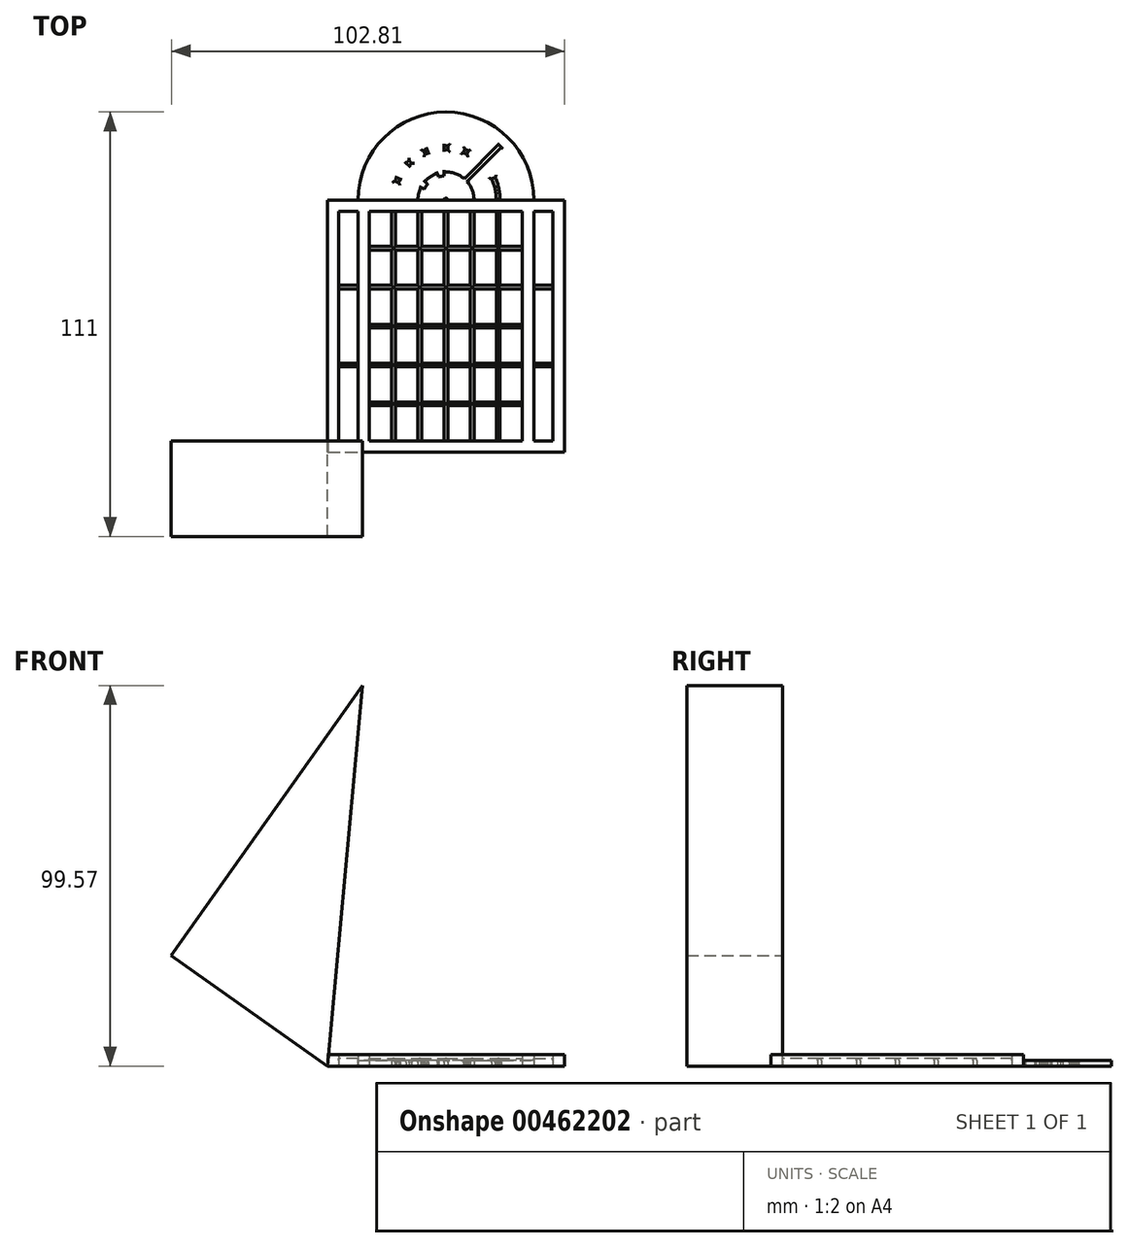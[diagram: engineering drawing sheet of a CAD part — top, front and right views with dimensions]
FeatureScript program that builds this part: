
annotation { "Feature Type Name" : "Feature", "Feature Type Description" : "" }
export const myFeature = defineFeature(function(context is Context, id is Id, definition is map)
    precondition{}
    {
        {
            var Q0;
            Q0=qCreatedBy(makeId("Top.planeOp"),FACE);
            var sketch = newSketch(context, id + "F0", { "sketchPlane" : qUnion([Q0])});
            skLineSegment(sketch, "E0.bottom", {"start": v(0, 0) * mm, "end": v(62, 0) * mm});
            skLineSegment(sketch, "E0.top", {"start": v(0, 60) * mm, "end": v(62, 60) * mm});
            skLineSegment(sketch, "E0.left", {"start": v(0, 0) * mm, "end": v(0, 60) * mm});
            skLineSegment(sketch, "E0.right", {"start": v(62, 0) * mm, "end": v(62, 60) * mm});
            skLineSegment(sketch, "E1", {"start": v(0, 0) * mm, "end": v(8, 0) * mm, "construction": true});
            skLineSegment(sketch, "E2", {"start": v(62, 0) * mm, "end": v(54, 0) * mm, "construction": true});
            skLineSegment(sketch, "E3", {"start": v(62, 0) * mm, "end": v(59, 0) * mm, "construction": true});
            skLineSegment(sketch, "E4", {"start": v(59, 0) * mm, "end": v(59, 60) * mm});
            skLineSegment(sketch, "E5", {"start": v(0, 60) * mm, "end": v(3, 60) * mm, "construction": true});
            skLineSegment(sketch, "E6", {"start": v(3, 60) * mm, "end": v(3, 0) * mm});
            skLineSegment(sketch, "E7", {"start": v(8, 0) * mm, "end": v(8, 60) * mm});
            skLineSegment(sketch, "E8", {"start": v(54, 0) * mm, "end": v(54, 60) * mm});
            skLineSegment(sketch, "E9", {"start": v(8, 0) * mm, "end": v(11, 0) * mm, "construction": true});
            skLineSegment(sketch, "E10", {"start": v(54, 0) * mm, "end": v(51, 0) * mm, "construction": true});
            skLineSegment(sketch, "E11", {"start": v(11, 0) * mm, "end": v(11, 60) * mm});
            skLineSegment(sketch, "E12", {"start": v(51, 0) * mm, "end": v(51, 60) * mm});
            skLineSegment(sketch, "E13.bottom", {"start": v(51, 0) * mm, "end": v(45.17, 0) * mm});
            skLineSegment(sketch, "E13.top", {"start": v(51, 9.17) * mm, "end": v(45.17, 9.17) * mm});
            skLineSegment(sketch, "E13.left", {"start": v(51, 0) * mm, "end": v(51, 9.17) * mm});
            skLineSegment(sketch, "E13.right", {"start": v(45.17, 0) * mm, "end": v(45.17, 9.17) * mm});
            skLineSegment(sketch, "E14.bottom", {"start": v(45.17, 0) * mm, "end": v(44.17, 0) * mm});
            skLineSegment(sketch, "E14.top", {"start": v(45.17, 9.17) * mm, "end": v(44.17, 9.17) * mm, "construction": true});
            skLineSegment(sketch, "E14.right", {"start": v(44.17, 0) * mm, "end": v(44.17, 9.17) * mm});
            skLineSegment(sketch, "E15.top", {"start": v(51, 10.17) * mm, "end": v(45.17, 10.17) * mm});
            skLineSegment(sketch, "E15.left", {"start": v(51, 9.17) * mm, "end": v(51, 10.17) * mm});
            skLineSegment(sketch, "E15.right", {"start": v(45.17, 9.17) * mm, "end": v(45.17, 10.17) * mm, "construction": true});
            skLineSegment(sketch, "E16", {"start": v(44.17, 9.17) * mm, "end": v(44.17, 10.17) * mm, "construction": true});
            skLineSegment(sketch, "E17", {"start": v(44.17, 10.17) * mm, "end": v(45.17, 10.17) * mm, "construction": true});
            skLineSegment(sketch, "E18.0.1.0", {"start": v(44.17, 20.33) * mm, "end": v(45.17, 20.33) * mm, "construction": true});
            skLineSegment(sketch, "E18.0.1.1", {"start": v(51, 20.33) * mm, "end": v(45.17, 20.33) * mm});
            skLineSegment(sketch, "E18.0.1.2", {"start": v(51, 19.33) * mm, "end": v(45.17, 19.33) * mm});
            skLineSegment(sketch, "E18.0.1.3", {"start": v(45.17, 10.17) * mm, "end": v(45.17, 19.33) * mm});
            skLineSegment(sketch, "E18.0.1.4", {"start": v(44.17, 10.17) * mm, "end": v(44.17, 19.33) * mm});
            skLineSegment(sketch, "E18.0.1.5", {"start": v(45.17, 19.33) * mm, "end": v(44.17, 19.33) * mm, "construction": true});
            skLineSegment(sketch, "E18.0.1.6", {"start": v(44.17, 19.33) * mm, "end": v(44.17, 20.33) * mm, "construction": true});
            skLineSegment(sketch, "E18.0.1.7", {"start": v(45.17, 19.33) * mm, "end": v(45.17, 20.33) * mm, "construction": true});
            skLineSegment(sketch, "E18.0.2.0", {"start": v(44.17, 30.5) * mm, "end": v(45.17, 30.5) * mm, "construction": true});
            skLineSegment(sketch, "E18.0.2.1", {"start": v(51, 30.5) * mm, "end": v(45.17, 30.5) * mm});
            skLineSegment(sketch, "E18.0.2.2", {"start": v(51, 29.5) * mm, "end": v(45.17, 29.5) * mm});
            skLineSegment(sketch, "E18.0.2.3", {"start": v(45.17, 20.33) * mm, "end": v(45.17, 29.5) * mm});
            skLineSegment(sketch, "E18.0.2.4", {"start": v(44.17, 20.33) * mm, "end": v(44.17, 29.5) * mm});
            skLineSegment(sketch, "E18.0.2.5", {"start": v(45.17, 29.5) * mm, "end": v(44.17, 29.5) * mm, "construction": true});
            skLineSegment(sketch, "E18.0.2.6", {"start": v(44.17, 29.5) * mm, "end": v(44.17, 30.5) * mm, "construction": true});
            skLineSegment(sketch, "E18.0.2.7", {"start": v(45.17, 29.5) * mm, "end": v(45.17, 30.5) * mm, "construction": true});
            skLineSegment(sketch, "E18.0.3.0", {"start": v(44.17, 40.67) * mm, "end": v(45.17, 40.67) * mm, "construction": true});
            skLineSegment(sketch, "E18.0.3.1", {"start": v(51, 40.67) * mm, "end": v(45.17, 40.67) * mm});
            skLineSegment(sketch, "E18.0.3.2", {"start": v(51, 39.67) * mm, "end": v(45.17, 39.67) * mm});
            skLineSegment(sketch, "E18.0.3.3", {"start": v(45.17, 30.5) * mm, "end": v(45.17, 39.67) * mm});
            skLineSegment(sketch, "E18.0.3.4", {"start": v(44.17, 30.5) * mm, "end": v(44.17, 39.67) * mm});
            skLineSegment(sketch, "E18.0.3.5", {"start": v(45.17, 39.67) * mm, "end": v(44.17, 39.67) * mm, "construction": true});
            skLineSegment(sketch, "E18.0.3.6", {"start": v(44.17, 39.67) * mm, "end": v(44.17, 40.67) * mm, "construction": true});
            skLineSegment(sketch, "E18.0.3.7", {"start": v(45.17, 39.67) * mm, "end": v(45.17, 40.67) * mm, "construction": true});
            skLineSegment(sketch, "E18.0.4.0", {"start": v(44.17, 50.83) * mm, "end": v(45.17, 50.83) * mm, "construction": true});
            skLineSegment(sketch, "E18.0.4.1", {"start": v(51, 50.83) * mm, "end": v(45.17, 50.83) * mm});
            skLineSegment(sketch, "E18.0.4.2", {"start": v(51, 49.83) * mm, "end": v(45.17, 49.83) * mm});
            skLineSegment(sketch, "E18.0.4.3", {"start": v(45.17, 40.67) * mm, "end": v(45.17, 49.83) * mm});
            skLineSegment(sketch, "E18.0.4.4", {"start": v(44.17, 40.67) * mm, "end": v(44.17, 49.83) * mm});
            skLineSegment(sketch, "E18.0.4.5", {"start": v(45.17, 49.83) * mm, "end": v(44.17, 49.83) * mm, "construction": true});
            skLineSegment(sketch, "E18.0.4.6", {"start": v(44.17, 49.83) * mm, "end": v(44.17, 50.83) * mm, "construction": true});
            skLineSegment(sketch, "E18.0.4.7", {"start": v(45.17, 49.83) * mm, "end": v(45.17, 50.83) * mm, "construction": true});
            skLineSegment(sketch, "E18.0.5.2", {"start": v(51, 60) * mm, "end": v(45.17, 60) * mm});
            skLineSegment(sketch, "E18.0.5.3", {"start": v(45.17, 50.83) * mm, "end": v(45.17, 60) * mm});
            skLineSegment(sketch, "E18.0.5.4", {"start": v(44.17, 50.83) * mm, "end": v(44.17, 60) * mm});
            skLineSegment(sketch, "E18.0.5.5", {"start": v(45.17, 60) * mm, "end": v(44.17, 60) * mm, "construction": true});
            skLineSegment(sketch, "E18.1.0.0", {"start": v(37.33, 10.17) * mm, "end": v(38.33, 10.17) * mm, "construction": true});
            skLineSegment(sketch, "E18.1.0.1", {"start": v(44.17, 10.17) * mm, "end": v(38.33, 10.17) * mm});
            skLineSegment(sketch, "E18.1.0.2", {"start": v(44.17, 9.17) * mm, "end": v(38.33, 9.17) * mm});
            skLineSegment(sketch, "E18.1.0.3", {"start": v(38.33, 0) * mm, "end": v(38.33, 9.17) * mm});
            skLineSegment(sketch, "E18.1.0.4", {"start": v(37.33, 0) * mm, "end": v(37.33, 9.17) * mm});
            skLineSegment(sketch, "E18.1.0.5", {"start": v(38.33, 9.17) * mm, "end": v(37.33, 9.17) * mm, "construction": true});
            skLineSegment(sketch, "E18.1.0.6", {"start": v(37.33, 9.17) * mm, "end": v(37.33, 10.17) * mm, "construction": true});
            skLineSegment(sketch, "E18.1.0.7", {"start": v(38.33, 9.17) * mm, "end": v(38.33, 10.17) * mm, "construction": true});
            skLineSegment(sketch, "E18.1.1.0", {"start": v(37.33, 20.33) * mm, "end": v(38.33, 20.33) * mm, "construction": true});
            skLineSegment(sketch, "E18.1.1.1", {"start": v(44.17, 20.33) * mm, "end": v(38.33, 20.33) * mm});
            skLineSegment(sketch, "E18.1.1.2", {"start": v(44.17, 19.33) * mm, "end": v(38.33, 19.33) * mm});
            skLineSegment(sketch, "E18.1.1.3", {"start": v(38.33, 10.17) * mm, "end": v(38.33, 19.33) * mm});
            skLineSegment(sketch, "E18.1.1.4", {"start": v(37.33, 10.17) * mm, "end": v(37.33, 19.33) * mm});
            skLineSegment(sketch, "E18.1.1.5", {"start": v(38.33, 19.33) * mm, "end": v(37.33, 19.33) * mm, "construction": true});
            skLineSegment(sketch, "E18.1.1.6", {"start": v(37.33, 19.33) * mm, "end": v(37.33, 20.33) * mm, "construction": true});
            skLineSegment(sketch, "E18.1.1.7", {"start": v(38.33, 19.33) * mm, "end": v(38.33, 20.33) * mm, "construction": true});
            skLineSegment(sketch, "E18.1.2.0", {"start": v(37.33, 30.5) * mm, "end": v(38.33, 30.5) * mm, "construction": true});
            skLineSegment(sketch, "E18.1.2.1", {"start": v(44.17, 30.5) * mm, "end": v(38.33, 30.5) * mm});
            skLineSegment(sketch, "E18.1.2.2", {"start": v(44.17, 29.5) * mm, "end": v(38.33, 29.5) * mm});
            skLineSegment(sketch, "E18.1.2.3", {"start": v(38.33, 20.33) * mm, "end": v(38.33, 29.5) * mm});
            skLineSegment(sketch, "E18.1.2.4", {"start": v(37.33, 20.33) * mm, "end": v(37.33, 29.5) * mm});
            skLineSegment(sketch, "E18.1.2.5", {"start": v(38.33, 29.5) * mm, "end": v(37.33, 29.5) * mm, "construction": true});
            skLineSegment(sketch, "E18.1.2.6", {"start": v(37.33, 29.5) * mm, "end": v(37.33, 30.5) * mm, "construction": true});
            skLineSegment(sketch, "E18.1.2.7", {"start": v(38.33, 29.5) * mm, "end": v(38.33, 30.5) * mm, "construction": true});
            skLineSegment(sketch, "E18.1.3.0", {"start": v(37.33, 40.67) * mm, "end": v(38.33, 40.67) * mm, "construction": true});
            skLineSegment(sketch, "E18.1.3.1", {"start": v(44.17, 40.67) * mm, "end": v(38.33, 40.67) * mm});
            skLineSegment(sketch, "E18.1.3.2", {"start": v(44.17, 39.67) * mm, "end": v(38.33, 39.67) * mm});
            skLineSegment(sketch, "E18.1.3.3", {"start": v(38.33, 30.5) * mm, "end": v(38.33, 39.67) * mm});
            skLineSegment(sketch, "E18.1.3.4", {"start": v(37.33, 30.5) * mm, "end": v(37.33, 39.67) * mm});
            skLineSegment(sketch, "E18.1.3.5", {"start": v(38.33, 39.67) * mm, "end": v(37.33, 39.67) * mm, "construction": true});
            skLineSegment(sketch, "E18.1.3.6", {"start": v(37.33, 39.67) * mm, "end": v(37.33, 40.67) * mm, "construction": true});
            skLineSegment(sketch, "E18.1.3.7", {"start": v(38.33, 39.67) * mm, "end": v(38.33, 40.67) * mm, "construction": true});
            skLineSegment(sketch, "E18.1.4.0", {"start": v(37.33, 50.83) * mm, "end": v(38.33, 50.83) * mm, "construction": true});
            skLineSegment(sketch, "E18.1.4.1", {"start": v(44.17, 50.83) * mm, "end": v(38.33, 50.83) * mm});
            skLineSegment(sketch, "E18.1.4.2", {"start": v(44.17, 49.83) * mm, "end": v(38.33, 49.83) * mm});
            skLineSegment(sketch, "E18.1.4.3", {"start": v(38.33, 40.67) * mm, "end": v(38.33, 49.83) * mm});
            skLineSegment(sketch, "E18.1.4.4", {"start": v(37.33, 40.67) * mm, "end": v(37.33, 49.83) * mm});
            skLineSegment(sketch, "E18.1.4.5", {"start": v(38.33, 49.83) * mm, "end": v(37.33, 49.83) * mm, "construction": true});
            skLineSegment(sketch, "E18.1.4.6", {"start": v(37.33, 49.83) * mm, "end": v(37.33, 50.83) * mm, "construction": true});
            skLineSegment(sketch, "E18.1.4.7", {"start": v(38.33, 49.83) * mm, "end": v(38.33, 50.83) * mm, "construction": true});
            skLineSegment(sketch, "E18.1.5.2", {"start": v(44.17, 60) * mm, "end": v(38.33, 60) * mm});
            skLineSegment(sketch, "E18.1.5.3", {"start": v(38.33, 50.83) * mm, "end": v(38.33, 60) * mm});
            skLineSegment(sketch, "E18.1.5.4", {"start": v(37.33, 50.83) * mm, "end": v(37.33, 60) * mm});
            skLineSegment(sketch, "E18.1.5.5", {"start": v(38.33, 60) * mm, "end": v(37.33, 60) * mm, "construction": true});
            skLineSegment(sketch, "E18.2.0.0", {"start": v(30.5, 10.17) * mm, "end": v(31.5, 10.17) * mm, "construction": true});
            skLineSegment(sketch, "E18.2.0.1", {"start": v(37.33, 10.17) * mm, "end": v(31.5, 10.17) * mm});
            skLineSegment(sketch, "E18.2.0.2", {"start": v(37.33, 9.17) * mm, "end": v(31.5, 9.17) * mm});
            skLineSegment(sketch, "E18.2.0.3", {"start": v(31.5, 0) * mm, "end": v(31.5, 9.17) * mm});
            skLineSegment(sketch, "E18.2.0.4", {"start": v(30.5, 0) * mm, "end": v(30.5, 9.17) * mm});
            skLineSegment(sketch, "E18.2.0.5", {"start": v(31.5, 9.17) * mm, "end": v(30.5, 9.17) * mm, "construction": true});
            skLineSegment(sketch, "E18.2.0.6", {"start": v(30.5, 9.17) * mm, "end": v(30.5, 10.17) * mm, "construction": true});
            skLineSegment(sketch, "E18.2.0.7", {"start": v(31.5, 9.17) * mm, "end": v(31.5, 10.17) * mm, "construction": true});
            skLineSegment(sketch, "E18.2.1.0", {"start": v(30.5, 20.33) * mm, "end": v(31.5, 20.33) * mm, "construction": true});
            skLineSegment(sketch, "E18.2.1.1", {"start": v(37.33, 20.33) * mm, "end": v(31.5, 20.33) * mm});
            skLineSegment(sketch, "E18.2.1.2", {"start": v(37.33, 19.33) * mm, "end": v(31.5, 19.33) * mm});
            skLineSegment(sketch, "E18.2.1.3", {"start": v(31.5, 10.17) * mm, "end": v(31.5, 19.33) * mm});
            skLineSegment(sketch, "E18.2.1.4", {"start": v(30.5, 10.17) * mm, "end": v(30.5, 19.33) * mm});
            skLineSegment(sketch, "E18.2.1.5", {"start": v(31.5, 19.33) * mm, "end": v(30.5, 19.33) * mm, "construction": true});
            skLineSegment(sketch, "E18.2.1.6", {"start": v(30.5, 19.33) * mm, "end": v(30.5, 20.33) * mm, "construction": true});
            skLineSegment(sketch, "E18.2.1.7", {"start": v(31.5, 19.33) * mm, "end": v(31.5, 20.33) * mm, "construction": true});
            skLineSegment(sketch, "E18.2.2.0", {"start": v(30.5, 30.5) * mm, "end": v(31.5, 30.5) * mm, "construction": true});
            skLineSegment(sketch, "E18.2.2.1", {"start": v(37.33, 30.5) * mm, "end": v(31.5, 30.5) * mm});
            skLineSegment(sketch, "E18.2.2.2", {"start": v(37.33, 29.5) * mm, "end": v(31.5, 29.5) * mm});
            skLineSegment(sketch, "E18.2.2.3", {"start": v(31.5, 20.33) * mm, "end": v(31.5, 29.5) * mm});
            skLineSegment(sketch, "E18.2.2.4", {"start": v(30.5, 20.33) * mm, "end": v(30.5, 29.5) * mm});
            skLineSegment(sketch, "E18.2.2.5", {"start": v(31.5, 29.5) * mm, "end": v(30.5, 29.5) * mm, "construction": true});
            skLineSegment(sketch, "E18.2.2.6", {"start": v(30.5, 29.5) * mm, "end": v(30.5, 30.5) * mm, "construction": true});
            skLineSegment(sketch, "E18.2.2.7", {"start": v(31.5, 29.5) * mm, "end": v(31.5, 30.5) * mm, "construction": true});
            skLineSegment(sketch, "E18.2.3.0", {"start": v(30.5, 40.67) * mm, "end": v(31.5, 40.67) * mm, "construction": true});
            skLineSegment(sketch, "E18.2.3.1", {"start": v(37.33, 40.67) * mm, "end": v(31.5, 40.67) * mm});
            skLineSegment(sketch, "E18.2.3.2", {"start": v(37.33, 39.67) * mm, "end": v(31.5, 39.67) * mm});
            skLineSegment(sketch, "E18.2.3.3", {"start": v(31.5, 30.5) * mm, "end": v(31.5, 39.67) * mm});
            skLineSegment(sketch, "E18.2.3.4", {"start": v(30.5, 30.5) * mm, "end": v(30.5, 39.67) * mm});
            skLineSegment(sketch, "E18.2.3.5", {"start": v(31.5, 39.67) * mm, "end": v(30.5, 39.67) * mm, "construction": true});
            skLineSegment(sketch, "E18.2.3.6", {"start": v(30.5, 39.67) * mm, "end": v(30.5, 40.67) * mm, "construction": true});
            skLineSegment(sketch, "E18.2.3.7", {"start": v(31.5, 39.67) * mm, "end": v(31.5, 40.67) * mm, "construction": true});
            skLineSegment(sketch, "E18.2.4.0", {"start": v(30.5, 50.83) * mm, "end": v(31.5, 50.83) * mm, "construction": true});
            skLineSegment(sketch, "E18.2.4.1", {"start": v(37.33, 50.83) * mm, "end": v(31.5, 50.83) * mm});
            skLineSegment(sketch, "E18.2.4.2", {"start": v(37.33, 49.83) * mm, "end": v(31.5, 49.83) * mm});
            skLineSegment(sketch, "E18.2.4.3", {"start": v(31.5, 40.67) * mm, "end": v(31.5, 49.83) * mm});
            skLineSegment(sketch, "E18.2.4.4", {"start": v(30.5, 40.67) * mm, "end": v(30.5, 49.83) * mm});
            skLineSegment(sketch, "E18.2.4.5", {"start": v(31.5, 49.83) * mm, "end": v(30.5, 49.83) * mm, "construction": true});
            skLineSegment(sketch, "E18.2.4.6", {"start": v(30.5, 49.83) * mm, "end": v(30.5, 50.83) * mm, "construction": true});
            skLineSegment(sketch, "E18.2.4.7", {"start": v(31.5, 49.83) * mm, "end": v(31.5, 50.83) * mm, "construction": true});
            skLineSegment(sketch, "E18.2.5.2", {"start": v(37.33, 60) * mm, "end": v(31.5, 60) * mm});
            skLineSegment(sketch, "E18.2.5.3", {"start": v(31.5, 50.83) * mm, "end": v(31.5, 60) * mm});
            skLineSegment(sketch, "E18.2.5.4", {"start": v(30.5, 50.83) * mm, "end": v(30.5, 60) * mm});
            skLineSegment(sketch, "E18.2.5.5", {"start": v(31.5, 60) * mm, "end": v(30.5, 60) * mm, "construction": true});
            skLineSegment(sketch, "E18.3.0.0", {"start": v(23.67, 10.17) * mm, "end": v(24.67, 10.17) * mm, "construction": true});
            skLineSegment(sketch, "E18.3.0.1", {"start": v(30.5, 10.17) * mm, "end": v(24.67, 10.17) * mm});
            skLineSegment(sketch, "E18.3.0.2", {"start": v(30.5, 9.17) * mm, "end": v(24.67, 9.17) * mm});
            skLineSegment(sketch, "E18.3.0.3", {"start": v(24.67, 0) * mm, "end": v(24.67, 9.17) * mm});
            skLineSegment(sketch, "E18.3.0.4", {"start": v(23.67, 0) * mm, "end": v(23.67, 9.17) * mm});
            skLineSegment(sketch, "E18.3.0.5", {"start": v(24.67, 9.17) * mm, "end": v(23.67, 9.17) * mm, "construction": true});
            skLineSegment(sketch, "E18.3.0.6", {"start": v(23.67, 9.17) * mm, "end": v(23.67, 10.17) * mm, "construction": true});
            skLineSegment(sketch, "E18.3.0.7", {"start": v(24.67, 9.17) * mm, "end": v(24.67, 10.17) * mm, "construction": true});
            skLineSegment(sketch, "E18.3.1.0", {"start": v(23.67, 20.33) * mm, "end": v(24.67, 20.33) * mm, "construction": true});
            skLineSegment(sketch, "E18.3.1.1", {"start": v(30.5, 20.33) * mm, "end": v(24.67, 20.33) * mm});
            skLineSegment(sketch, "E18.3.1.2", {"start": v(30.5, 19.33) * mm, "end": v(24.67, 19.33) * mm});
            skLineSegment(sketch, "E18.3.1.3", {"start": v(24.67, 10.17) * mm, "end": v(24.67, 19.33) * mm});
            skLineSegment(sketch, "E18.3.1.4", {"start": v(23.67, 10.17) * mm, "end": v(23.67, 19.33) * mm});
            skLineSegment(sketch, "E18.3.1.5", {"start": v(24.67, 19.33) * mm, "end": v(23.67, 19.33) * mm, "construction": true});
            skLineSegment(sketch, "E18.3.1.6", {"start": v(23.67, 19.33) * mm, "end": v(23.67, 20.33) * mm, "construction": true});
            skLineSegment(sketch, "E18.3.1.7", {"start": v(24.67, 19.33) * mm, "end": v(24.67, 20.33) * mm, "construction": true});
            skLineSegment(sketch, "E18.3.2.0", {"start": v(23.67, 30.5) * mm, "end": v(24.67, 30.5) * mm, "construction": true});
            skLineSegment(sketch, "E18.3.2.1", {"start": v(30.5, 30.5) * mm, "end": v(24.67, 30.5) * mm});
            skLineSegment(sketch, "E18.3.2.2", {"start": v(30.5, 29.5) * mm, "end": v(24.67, 29.5) * mm});
            skLineSegment(sketch, "E18.3.2.3", {"start": v(24.67, 20.33) * mm, "end": v(24.67, 29.5) * mm});
            skLineSegment(sketch, "E18.3.2.4", {"start": v(23.67, 20.33) * mm, "end": v(23.67, 29.5) * mm});
            skLineSegment(sketch, "E18.3.2.5", {"start": v(24.67, 29.5) * mm, "end": v(23.67, 29.5) * mm, "construction": true});
            skLineSegment(sketch, "E18.3.2.6", {"start": v(23.67, 29.5) * mm, "end": v(23.67, 30.5) * mm, "construction": true});
            skLineSegment(sketch, "E18.3.2.7", {"start": v(24.67, 29.5) * mm, "end": v(24.67, 30.5) * mm, "construction": true});
            skLineSegment(sketch, "E18.3.3.0", {"start": v(23.67, 40.67) * mm, "end": v(24.67, 40.67) * mm, "construction": true});
            skLineSegment(sketch, "E18.3.3.1", {"start": v(30.5, 40.67) * mm, "end": v(24.67, 40.67) * mm});
            skLineSegment(sketch, "E18.3.3.2", {"start": v(30.5, 39.67) * mm, "end": v(24.67, 39.67) * mm});
            skLineSegment(sketch, "E18.3.3.3", {"start": v(24.67, 30.5) * mm, "end": v(24.67, 39.67) * mm});
            skLineSegment(sketch, "E18.3.3.4", {"start": v(23.67, 30.5) * mm, "end": v(23.67, 39.67) * mm});
            skLineSegment(sketch, "E18.3.3.5", {"start": v(24.67, 39.67) * mm, "end": v(23.67, 39.67) * mm, "construction": true});
            skLineSegment(sketch, "E18.3.3.6", {"start": v(23.67, 39.67) * mm, "end": v(23.67, 40.67) * mm, "construction": true});
            skLineSegment(sketch, "E18.3.3.7", {"start": v(24.67, 39.67) * mm, "end": v(24.67, 40.67) * mm, "construction": true});
            skLineSegment(sketch, "E18.3.4.0", {"start": v(23.67, 50.83) * mm, "end": v(24.67, 50.83) * mm, "construction": true});
            skLineSegment(sketch, "E18.3.4.1", {"start": v(30.5, 50.83) * mm, "end": v(24.67, 50.83) * mm});
            skLineSegment(sketch, "E18.3.4.2", {"start": v(30.5, 49.83) * mm, "end": v(24.67, 49.83) * mm});
            skLineSegment(sketch, "E18.3.4.3", {"start": v(24.67, 40.67) * mm, "end": v(24.67, 49.83) * mm});
            skLineSegment(sketch, "E18.3.4.4", {"start": v(23.67, 40.67) * mm, "end": v(23.67, 49.83) * mm});
            skLineSegment(sketch, "E18.3.4.5", {"start": v(24.67, 49.83) * mm, "end": v(23.67, 49.83) * mm, "construction": true});
            skLineSegment(sketch, "E18.3.4.6", {"start": v(23.67, 49.83) * mm, "end": v(23.67, 50.83) * mm, "construction": true});
            skLineSegment(sketch, "E18.3.4.7", {"start": v(24.67, 49.83) * mm, "end": v(24.67, 50.83) * mm, "construction": true});
            skLineSegment(sketch, "E18.3.5.2", {"start": v(30.5, 60) * mm, "end": v(24.67, 60) * mm});
            skLineSegment(sketch, "E18.3.5.3", {"start": v(24.67, 50.83) * mm, "end": v(24.67, 60) * mm});
            skLineSegment(sketch, "E18.3.5.4", {"start": v(23.67, 50.83) * mm, "end": v(23.67, 60) * mm});
            skLineSegment(sketch, "E18.3.5.5", {"start": v(24.67, 60) * mm, "end": v(23.67, 60) * mm, "construction": true});
            skLineSegment(sketch, "E18.4.0.0", {"start": v(16.83, 10.17) * mm, "end": v(17.83, 10.17) * mm, "construction": true});
            skLineSegment(sketch, "E18.4.0.1", {"start": v(23.67, 10.17) * mm, "end": v(17.83, 10.17) * mm});
            skLineSegment(sketch, "E18.4.0.2", {"start": v(23.67, 9.17) * mm, "end": v(17.83, 9.17) * mm});
            skLineSegment(sketch, "E18.4.0.3", {"start": v(17.83, 0) * mm, "end": v(17.83, 9.17) * mm});
            skLineSegment(sketch, "E18.4.0.4", {"start": v(16.83, 0) * mm, "end": v(16.83, 9.17) * mm});
            skLineSegment(sketch, "E18.4.0.5", {"start": v(17.83, 9.17) * mm, "end": v(16.83, 9.17) * mm, "construction": true});
            skLineSegment(sketch, "E18.4.0.6", {"start": v(16.83, 9.17) * mm, "end": v(16.83, 10.17) * mm, "construction": true});
            skLineSegment(sketch, "E18.4.0.7", {"start": v(17.83, 9.17) * mm, "end": v(17.83, 10.17) * mm, "construction": true});
            skLineSegment(sketch, "E18.4.1.0", {"start": v(16.83, 20.33) * mm, "end": v(17.83, 20.33) * mm, "construction": true});
            skLineSegment(sketch, "E18.4.1.1", {"start": v(23.67, 20.33) * mm, "end": v(17.83, 20.33) * mm});
            skLineSegment(sketch, "E18.4.1.2", {"start": v(23.67, 19.33) * mm, "end": v(17.83, 19.33) * mm});
            skLineSegment(sketch, "E18.4.1.3", {"start": v(17.83, 10.17) * mm, "end": v(17.83, 19.33) * mm});
            skLineSegment(sketch, "E18.4.1.4", {"start": v(16.83, 10.17) * mm, "end": v(16.83, 19.33) * mm});
            skLineSegment(sketch, "E18.4.1.5", {"start": v(17.83, 19.33) * mm, "end": v(16.83, 19.33) * mm, "construction": true});
            skLineSegment(sketch, "E18.4.1.6", {"start": v(16.83, 19.33) * mm, "end": v(16.83, 20.33) * mm, "construction": true});
            skLineSegment(sketch, "E18.4.1.7", {"start": v(17.83, 19.33) * mm, "end": v(17.83, 20.33) * mm, "construction": true});
            skLineSegment(sketch, "E18.4.2.0", {"start": v(16.83, 30.5) * mm, "end": v(17.83, 30.5) * mm, "construction": true});
            skLineSegment(sketch, "E18.4.2.1", {"start": v(23.67, 30.5) * mm, "end": v(17.83, 30.5) * mm});
            skLineSegment(sketch, "E18.4.2.2", {"start": v(23.67, 29.5) * mm, "end": v(17.83, 29.5) * mm});
            skLineSegment(sketch, "E18.4.2.3", {"start": v(17.83, 20.33) * mm, "end": v(17.83, 29.5) * mm});
            skLineSegment(sketch, "E18.4.2.4", {"start": v(16.83, 20.33) * mm, "end": v(16.83, 29.5) * mm});
            skLineSegment(sketch, "E18.4.2.5", {"start": v(17.83, 29.5) * mm, "end": v(16.83, 29.5) * mm, "construction": true});
            skLineSegment(sketch, "E18.4.2.6", {"start": v(16.83, 29.5) * mm, "end": v(16.83, 30.5) * mm, "construction": true});
            skLineSegment(sketch, "E18.4.2.7", {"start": v(17.83, 29.5) * mm, "end": v(17.83, 30.5) * mm, "construction": true});
            skLineSegment(sketch, "E18.4.3.0", {"start": v(16.83, 40.67) * mm, "end": v(17.83, 40.67) * mm, "construction": true});
            skLineSegment(sketch, "E18.4.3.1", {"start": v(23.67, 40.67) * mm, "end": v(17.83, 40.67) * mm});
            skLineSegment(sketch, "E18.4.3.2", {"start": v(23.67, 39.67) * mm, "end": v(17.83, 39.67) * mm});
            skLineSegment(sketch, "E18.4.3.3", {"start": v(17.83, 30.5) * mm, "end": v(17.83, 39.67) * mm});
            skLineSegment(sketch, "E18.4.3.4", {"start": v(16.83, 30.5) * mm, "end": v(16.83, 39.67) * mm});
            skLineSegment(sketch, "E18.4.3.5", {"start": v(17.83, 39.67) * mm, "end": v(16.83, 39.67) * mm, "construction": true});
            skLineSegment(sketch, "E18.4.3.6", {"start": v(16.83, 39.67) * mm, "end": v(16.83, 40.67) * mm, "construction": true});
            skLineSegment(sketch, "E18.4.3.7", {"start": v(17.83, 39.67) * mm, "end": v(17.83, 40.67) * mm, "construction": true});
            skLineSegment(sketch, "E18.4.4.0", {"start": v(16.83, 50.83) * mm, "end": v(17.83, 50.83) * mm, "construction": true});
            skLineSegment(sketch, "E18.4.4.1", {"start": v(23.67, 50.83) * mm, "end": v(17.83, 50.83) * mm});
            skLineSegment(sketch, "E18.4.4.2", {"start": v(23.67, 49.83) * mm, "end": v(17.83, 49.83) * mm});
            skLineSegment(sketch, "E18.4.4.3", {"start": v(17.83, 40.67) * mm, "end": v(17.83, 49.83) * mm});
            skLineSegment(sketch, "E18.4.4.4", {"start": v(16.83, 40.67) * mm, "end": v(16.83, 49.83) * mm});
            skLineSegment(sketch, "E18.4.4.5", {"start": v(17.83, 49.83) * mm, "end": v(16.83, 49.83) * mm, "construction": true});
            skLineSegment(sketch, "E18.4.4.6", {"start": v(16.83, 49.83) * mm, "end": v(16.83, 50.83) * mm, "construction": true});
            skLineSegment(sketch, "E18.4.4.7", {"start": v(17.83, 49.83) * mm, "end": v(17.83, 50.83) * mm, "construction": true});
            skLineSegment(sketch, "E18.4.5.2", {"start": v(23.67, 60) * mm, "end": v(17.83, 60) * mm});
            skLineSegment(sketch, "E18.4.5.3", {"start": v(17.83, 50.83) * mm, "end": v(17.83, 60) * mm});
            skLineSegment(sketch, "E18.4.5.4", {"start": v(16.83, 50.83) * mm, "end": v(16.83, 60) * mm});
            skLineSegment(sketch, "E18.4.5.5", {"start": v(17.83, 60) * mm, "end": v(16.83, 60) * mm, "construction": true});
            skLineSegment(sketch, "E18.5.0.1", {"start": v(16.83, 10.17) * mm, "end": v(11, 10.17) * mm});
            skLineSegment(sketch, "E18.5.0.2", {"start": v(16.83, 9.17) * mm, "end": v(11, 9.17) * mm});
            skLineSegment(sketch, "E18.5.0.3", {"start": v(11, 0) * mm, "end": v(11, 9.17) * mm});
            skLineSegment(sketch, "E18.5.0.7", {"start": v(11, 9.17) * mm, "end": v(11, 10.17) * mm, "construction": true});
            skLineSegment(sketch, "E18.5.1.1", {"start": v(16.83, 20.33) * mm, "end": v(11, 20.33) * mm});
            skLineSegment(sketch, "E18.5.1.2", {"start": v(16.83, 19.33) * mm, "end": v(11, 19.33) * mm});
            skLineSegment(sketch, "E18.5.1.3", {"start": v(11, 10.17) * mm, "end": v(11, 19.33) * mm});
            skLineSegment(sketch, "E18.5.1.7", {"start": v(11, 19.33) * mm, "end": v(11, 20.33) * mm, "construction": true});
            skLineSegment(sketch, "E18.5.2.1", {"start": v(16.83, 30.5) * mm, "end": v(11, 30.5) * mm});
            skLineSegment(sketch, "E18.5.2.2", {"start": v(16.83, 29.5) * mm, "end": v(11, 29.5) * mm});
            skLineSegment(sketch, "E18.5.2.3", {"start": v(11, 20.33) * mm, "end": v(11, 29.5) * mm});
            skLineSegment(sketch, "E18.5.2.7", {"start": v(11, 29.5) * mm, "end": v(11, 30.5) * mm, "construction": true});
            skLineSegment(sketch, "E18.5.3.1", {"start": v(16.83, 40.67) * mm, "end": v(11, 40.67) * mm});
            skLineSegment(sketch, "E18.5.3.2", {"start": v(16.83, 39.67) * mm, "end": v(11, 39.67) * mm});
            skLineSegment(sketch, "E18.5.3.3", {"start": v(11, 30.5) * mm, "end": v(11, 39.67) * mm});
            skLineSegment(sketch, "E18.5.3.7", {"start": v(11, 39.67) * mm, "end": v(11, 40.67) * mm, "construction": true});
            skLineSegment(sketch, "E18.5.4.1", {"start": v(16.83, 50.83) * mm, "end": v(11, 50.83) * mm});
            skLineSegment(sketch, "E18.5.4.2", {"start": v(16.83, 49.83) * mm, "end": v(11, 49.83) * mm});
            skLineSegment(sketch, "E18.5.4.3", {"start": v(11, 40.67) * mm, "end": v(11, 49.83) * mm});
            skLineSegment(sketch, "E18.5.4.7", {"start": v(11, 49.83) * mm, "end": v(11, 50.83) * mm, "construction": true});
            skLineSegment(sketch, "E18.5.5.2", {"start": v(16.83, 60) * mm, "end": v(11, 60) * mm});
            skLineSegment(sketch, "E18.5.5.3", {"start": v(11, 50.83) * mm, "end": v(11, 60) * mm});
            skLineSegment(sketch, "E18.direction1", {"start": v(44.17, 0) * mm, "end": v(37.33, 0) * mm, "construction": true});
            skLineSegment(sketch, "E18.direction2", {"start": v(44.17, 0) * mm, "end": v(44.17, 10.17) * mm, "construction": true});
            skLineSegment(sketch, "E19.top", {"start": v(0, -3) * mm, "end": v(62, -3) * mm});
            skLineSegment(sketch, "E19.left", {"start": v(0, 0) * mm, "end": v(0, -3) * mm});
            skLineSegment(sketch, "E19.right", {"start": v(62, 0) * mm, "end": v(62, -3) * mm});
            skLineSegment(sketch, "E20.top", {"start": v(0, 63) * mm, "end": v(62, 63) * mm});
            skLineSegment(sketch, "E20.left", {"start": v(0, 60) * mm, "end": v(0, 63) * mm});
            skLineSegment(sketch, "E20.right", {"start": v(62, 60) * mm, "end": v(62, 63) * mm});
            skLineSegment(sketch, "E21", {"start": v(31, 63) * mm, "end": v(31, 86) * mm, "construction": true});
            skArc(sketch, "E22", {"start": v(11, 63) * mm, "mid": v(31, 83) * mm, "end": v(51, 63) * mm});
            skArc(sketch, "E23", {"start": v(8, 63) * mm, "mid": v(31, 86) * mm, "end": v(54, 63) * mm});
            skArc(sketch, "E24", {"start": v(16.83, 63) * mm, "mid": v(31, 77.17) * mm, "end": v(45.17, 63) * mm});
            skArc(sketch, "E25", {"start": v(17.83, 63) * mm, "mid": v(31, 76.17) * mm, "end": v(44.17, 63) * mm});
            skArc(sketch, "E26", {"start": v(23.67, 63) * mm, "mid": v(31, 70.33) * mm, "end": v(38.33, 63) * mm});
            skArc(sketch, "E27", {"start": v(24.67, 63) * mm, "mid": v(31, 69.33) * mm, "end": v(37.33, 63) * mm});
            skArc(sketch, "E28", {"start": v(30.5, 63) * mm, "mid": v(31, 63.5) * mm, "end": v(31.5, 63) * mm});
            skLineSegment(sketch, "E29", {"start": v(31, 63) * mm, "end": v(8, 63) * mm});
            skLineSegment(sketch, "E30.1.0", {"start": v(31, 63) * mm, "end": v(9.75, 71.8) * mm, "construction": true});
            skLineSegment(sketch, "E30.2.0", {"start": v(31, 63) * mm, "end": v(14.74, 79.26) * mm, "construction": true});
            skLineSegment(sketch, "E30.3.0", {"start": v(31, 63) * mm, "end": v(22.2, 84.25) * mm, "construction": true});
            skLineSegment(sketch, "E30.5.0", {"start": v(31, 63) * mm, "end": v(39.8, 84.25) * mm, "construction": true});
            skLineSegment(sketch, "E30.6.0", {"start": v(31, 63) * mm, "end": v(47.26, 79.26) * mm, "construction": true});
            skLineSegment(sketch, "E30.7.0", {"start": v(31, 63) * mm, "end": v(52.25, 71.8) * mm, "construction": true});
            skLineSegment(sketch, "E30.8.0", {"start": v(31, 63) * mm, "end": v(54, 63) * mm});
            skLineSegment(sketch, "E30.anchor1", {"start": v(31, 63) * mm, "end": v(8, 63) * mm, "construction": true});
            skLineSegment(sketch, "E30.anchor2", {"start": v(31, 63) * mm, "end": v(54, 63) * mm, "construction": true});
            skLineSegment(sketch, "E31.0", {"start": v(30.08, 63.92) * mm, "end": v(12.72, 71.11) * mm});
            skLineSegment(sketch, "E32.MirrorCS", {"start": v(29.7, 63) * mm, "end": v(12.34, 70.19) * mm});
            skLineSegment(sketch, "E33.0", {"start": v(30.5, 64.2) * mm, "end": v(17.22, 77.5) * mm});
            skLineSegment(sketch, "E34.MirrorCS", {"start": v(28.87, 64.42) * mm, "end": v(16.5, 76.78) * mm});
            skLineSegment(sketch, "E35.0", {"start": v(31, 64.3) * mm, "end": v(23.81, 81.66) * mm});
            skLineSegment(sketch, "E36.MirrorCS", {"start": v(30.08, 63.92) * mm, "end": v(22.89, 81.28) * mm});
            skLineSegment(sketch, "E37.0", {"start": v(31.5, 65.51) * mm, "end": v(31.5, 83) * mm});
            skLineSegment(sketch, "E38.0", {"start": v(30.5, 65.51) * mm, "end": v(30.5, 83) * mm});
            skLineSegment(sketch, "E39.0", {"start": v(32.42, 65.13) * mm, "end": v(39.11, 81.28) * mm});
            skLineSegment(sketch, "E40.0", {"start": v(31, 64.3) * mm, "end": v(38.19, 81.66) * mm});
            skLineSegment(sketch, "E41.0", {"start": v(32.3, 63) * mm, "end": v(49.66, 70.19) * mm});
            skLineSegment(sketch, "E42.0", {"start": v(33.13, 64.42) * mm, "end": v(49.28, 71.11) * mm});
            skLineSegment(sketch, "E43.0", {"start": v(33.13, 64.42) * mm, "end": v(45.5, 76.78) * mm});
            skLineSegment(sketch, "E44.0", {"start": v(32.42, 65.13) * mm, "end": v(44.78, 77.5) * mm});
            skSolve(sketch);
        }
        {
            var Q0;
            {var subQ10=sQuery(id+"F0.wireOp",EDGE,"E23");Q0=makeQuery(id+"F0.imprint","IMPRINT",FACE,{"disambiguationData":[TD([[makeQuery(id+"F0.imprint","IMPRINT",EDGE,{"derivedFrom":subQ10}),-1.0]])]});}
            var Q1;
            {var subQ22=sQuery(id+"F0.wireOp",EDGE,"E20.left");Q1=makeQuery(id+"F0.imprint","IMPRINT",FACE,{"disambiguationData":[TD([[makeQuery(id+"F0.imprint","IMPRINT",EDGE,{"derivedFrom":subQ22}),-1.0]])]});}
            var Q2;
            {var subQ0=sQuery(id+"F0.wireOp",EDGE,"E0.right");Q2=makeQuery(id+"F0.imprint","IMPRINT",FACE,{"disambiguationData":[TD([[makeQuery(id+"F0.imprint","IMPRINT",EDGE,{"derivedFrom":subQ0}),1.0]])]});}
            var Q3;
            {var subQ14=sQuery(id+"F0.wireOp",EDGE,"E7");Q3=makeQuery(id+"F0.imprint","IMPRINT",FACE,{"disambiguationData":[TD([[makeQuery(id+"F0.imprint","IMPRINT",EDGE,{"derivedFrom":subQ14}),-1.0]])]});}
            var Q4;
            {var subQ0=sQuery(id+"F0.wireOp",EDGE,"E0.left");Q4=makeQuery(id+"F0.imprint","IMPRINT",FACE,{"disambiguationData":[TD([[makeQuery(id+"F0.imprint","IMPRINT",EDGE,{"derivedFrom":subQ0}),-1.0]])]});}
            var Q5;
            {var subQ5=sQuery(id+"F0.wireOp",EDGE,"E8");Q5=makeQuery(id+"F0.imprint","IMPRINT",FACE,{"disambiguationData":[TD([[makeQuery(id+"F0.imprint","IMPRINT",EDGE,{"derivedFrom":subQ5}),1.0]])]});}
            var Q6;
            Q6=makeQuery(id+"F0.imprint","IMPRINT",FACE,{"disambiguationData":[TD([[makeQuery(id+"F0.imprint","IMPRINT",EDGE,{"derivedFrom":sQuery(id+"F0.wireOp",EDGE,"E19.top")}),1.0]])]});
            extrude(context, id + "F1", {"entities" : qUnion([Q0, Q1, Q2, Q3, Q4, Q5, Q6]), "depth" : 3 * mm});
        }
        {
            var Q0;
            {var subQ0=sQuery(id+"F0.wireOp",EDGE,"E24");var subQ1=sQuery(id+"F0.wireOp",EDGE,"E20.top");var subQ2=makeQuery(id+"F0.imprint","INTERSECT",VERTEX,{"disambiguationData":[OD(0.0)],"derivedFrom":[subQ1,subQ0]});Q0=makeQuery(id+"F0.imprint","IMPRINT",FACE,{"disambiguationData":[TD([[makeQuery(id+"F0.imprint","IMPRINT",EDGE,{"disambiguationData":[TD([[subQ2,-1.0]])],"derivedFrom":subQ1}),1.0]])]});}
            var Q1;
            {var subQ0=sQuery(id+"F0.wireOp",EDGE,"E31.0");var subQ1=sQuery(id+"F0.wireOp",EDGE,"E24");var subQ2=makeQuery(id+"F0.imprint","INTERSECT",VERTEX,{"derivedFrom":[subQ1,subQ0]});Q1=makeQuery(id+"F0.imprint","IMPRINT",FACE,{"disambiguationData":[TD([[makeQuery(id+"F0.imprint","IMPRINT",EDGE,{"disambiguationData":[TD([[subQ2,-1.0]])],"derivedFrom":subQ1}),-1.0]])]});}
            var Q2;
            {var subQ0=sQuery(id+"F0.wireOp",EDGE,"E35.0");var subQ1=sQuery(id+"F0.wireOp",EDGE,"E24");var subQ2=makeQuery(id+"F0.imprint","INTERSECT",VERTEX,{"derivedFrom":[subQ1,subQ0]});Q2=makeQuery(id+"F0.imprint","IMPRINT",FACE,{"disambiguationData":[TD([[makeQuery(id+"F0.imprint","IMPRINT",EDGE,{"disambiguationData":[TD([[subQ2,-1.0]])],"derivedFrom":subQ1}),-1.0]])]});}
            var Q3;
            {var subQ0=sQuery(id+"F0.wireOp",EDGE,"E37.0");var subQ1=sQuery(id+"F0.wireOp",EDGE,"E24");var subQ2=makeQuery(id+"F0.imprint","INTERSECT",VERTEX,{"derivedFrom":[subQ1,subQ0]});Q3=makeQuery(id+"F0.imprint","IMPRINT",FACE,{"disambiguationData":[TD([[makeQuery(id+"F0.imprint","IMPRINT",EDGE,{"disambiguationData":[TD([[subQ2,-1.0]])],"derivedFrom":subQ1}),-1.0]])]});}
            var Q4;
            {var subQ0=sQuery(id+"F0.wireOp",EDGE,"E39.0");var subQ1=sQuery(id+"F0.wireOp",EDGE,"E24");var subQ2=makeQuery(id+"F0.imprint","INTERSECT",VERTEX,{"derivedFrom":[subQ1,subQ0]});Q4=makeQuery(id+"F0.imprint","IMPRINT",FACE,{"disambiguationData":[TD([[makeQuery(id+"F0.imprint","IMPRINT",EDGE,{"disambiguationData":[TD([[subQ2,-1.0]])],"derivedFrom":subQ1}),-1.0]])]});}
            var Q5;
            {var subQ0=sQuery(id+"F0.wireOp",EDGE,"E42.0");var subQ1=sQuery(id+"F0.wireOp",EDGE,"E24");var subQ2=makeQuery(id+"F0.imprint","INTERSECT",VERTEX,{"derivedFrom":[subQ1,subQ0]});Q5=makeQuery(id+"F0.imprint","IMPRINT",FACE,{"disambiguationData":[TD([[makeQuery(id+"F0.imprint","IMPRINT",EDGE,{"disambiguationData":[TD([[subQ2,1.0]])],"derivedFrom":subQ1}),-1.0]])]});}
            var Q6;
            {var subQ0=sQuery(id+"F0.wireOp",EDGE,"E24");var subQ1=sQuery(id+"F0.wireOp",EDGE,"E20.top");var subQ2=makeQuery(id+"F0.imprint","INTERSECT",VERTEX,{"disambiguationData":[OD(1.0)],"derivedFrom":[subQ1,subQ0]});Q6=makeQuery(id+"F0.imprint","IMPRINT",FACE,{"disambiguationData":[TD([[makeQuery(id+"F0.imprint","IMPRINT",EDGE,{"disambiguationData":[TD([[subQ2,1.0]])],"derivedFrom":subQ1}),1.0]])]});}
            var Q7;
            {var subQ0=sQuery(id+"F0.wireOp",EDGE,"E34.MirrorCS");var subQ1=sQuery(id+"F0.wireOp",EDGE,"E22");var subQ2=makeQuery(id+"F0.imprint","INTERSECT",VERTEX,{"derivedFrom":[subQ1,subQ0]});Q7=makeQuery(id+"F0.imprint","IMPRINT",FACE,{"disambiguationData":[TD([[makeQuery(id+"F0.imprint","IMPRINT",EDGE,{"disambiguationData":[TD([[subQ2,-1.0]])],"derivedFrom":subQ1}),-1.0]])]});}
            var Q8;
            {var subQ0=sQuery(id+"F0.wireOp",EDGE,"E32.MirrorCS");var subQ1=sQuery(id+"F0.wireOp",EDGE,"E22");var subQ2=makeQuery(id+"F0.imprint","INTERSECT",VERTEX,{"derivedFrom":[subQ1,subQ0]});Q8=makeQuery(id+"F0.imprint","IMPRINT",FACE,{"disambiguationData":[TD([[makeQuery(id+"F0.imprint","IMPRINT",EDGE,{"disambiguationData":[TD([[subQ2,-1.0]])],"derivedFrom":subQ1}),-1.0]])]});}
            var Q9;
            {var subQ0=sQuery(id+"F0.wireOp",EDGE,"E36.MirrorCS");var subQ1=sQuery(id+"F0.wireOp",EDGE,"E22");var subQ2=makeQuery(id+"F0.imprint","INTERSECT",VERTEX,{"derivedFrom":[subQ1,subQ0]});Q9=makeQuery(id+"F0.imprint","IMPRINT",FACE,{"disambiguationData":[TD([[makeQuery(id+"F0.imprint","IMPRINT",EDGE,{"disambiguationData":[TD([[subQ2,-1.0]])],"derivedFrom":subQ1}),-1.0]])]});}
            var Q10;
            {var subQ0=sQuery(id+"F0.wireOp",EDGE,"E38.0");var subQ1=sQuery(id+"F0.wireOp",EDGE,"E22");var subQ2=makeQuery(id+"F0.imprint","INTERSECT",VERTEX,{"derivedFrom":[subQ1,subQ0]});Q10=makeQuery(id+"F0.imprint","IMPRINT",FACE,{"disambiguationData":[TD([[makeQuery(id+"F0.imprint","IMPRINT",EDGE,{"disambiguationData":[TD([[subQ2,-1.0]])],"derivedFrom":subQ1}),-1.0]])]});}
            var Q11;
            {var subQ0=sQuery(id+"F0.wireOp",EDGE,"E40.0");var subQ1=sQuery(id+"F0.wireOp",EDGE,"E22");var subQ2=makeQuery(id+"F0.imprint","INTERSECT",VERTEX,{"derivedFrom":[subQ1,subQ0]});Q11=makeQuery(id+"F0.imprint","IMPRINT",FACE,{"disambiguationData":[TD([[makeQuery(id+"F0.imprint","IMPRINT",EDGE,{"disambiguationData":[TD([[subQ2,-1.0]])],"derivedFrom":subQ1}),-1.0]])]});}
            var Q12;
            {var subQ0=sQuery(id+"F0.wireOp",EDGE,"E44.0");var subQ1=sQuery(id+"F0.wireOp",EDGE,"E22");var subQ2=makeQuery(id+"F0.imprint","INTERSECT",VERTEX,{"derivedFrom":[subQ1,subQ0]});Q12=makeQuery(id+"F0.imprint","IMPRINT",FACE,{"disambiguationData":[TD([[makeQuery(id+"F0.imprint","IMPRINT",EDGE,{"disambiguationData":[TD([[subQ2,-1.0]])],"derivedFrom":subQ1}),-1.0]])]});}
            var Q13;
            {var subQ0=sQuery(id+"F0.wireOp",EDGE,"E42.0");var subQ1=sQuery(id+"F0.wireOp",EDGE,"E22");var subQ2=makeQuery(id+"F0.imprint","INTERSECT",VERTEX,{"derivedFrom":[subQ1,subQ0]});Q13=makeQuery(id+"F0.imprint","IMPRINT",FACE,{"disambiguationData":[TD([[makeQuery(id+"F0.imprint","IMPRINT",EDGE,{"disambiguationData":[TD([[subQ2,-1.0]])],"derivedFrom":subQ1}),-1.0]])]});}
            var Q14;
            {var subQ0=sQuery(id+"F0.wireOp",EDGE,"E41.0");var subQ1=sQuery(id+"F0.wireOp",EDGE,"E24");var subQ2=makeQuery(id+"F0.imprint","INTERSECT",VERTEX,{"derivedFrom":[subQ1,subQ0]});Q14=makeQuery(id+"F0.imprint","IMPRINT",FACE,{"disambiguationData":[TD([[makeQuery(id+"F0.imprint","IMPRINT",EDGE,{"disambiguationData":[TD([[subQ2,1.0]])],"derivedFrom":subQ1}),-1.0]])]});}
            var Q15;
            {var subQ0=sQuery(id+"F0.wireOp",EDGE,"E43.0");var subQ1=sQuery(id+"F0.wireOp",EDGE,"E24");var subQ2=makeQuery(id+"F0.imprint","INTERSECT",VERTEX,{"derivedFrom":[subQ1,subQ0]});Q15=makeQuery(id+"F0.imprint","IMPRINT",FACE,{"disambiguationData":[TD([[makeQuery(id+"F0.imprint","IMPRINT",EDGE,{"disambiguationData":[TD([[subQ2,1.0]])],"derivedFrom":subQ1}),-1.0]])]});}
            var Q16;
            {var subQ0=sQuery(id+"F0.wireOp",EDGE,"E39.0");var subQ1=sQuery(id+"F0.wireOp",EDGE,"E24");var subQ2=makeQuery(id+"F0.imprint","INTERSECT",VERTEX,{"derivedFrom":[subQ1,subQ0]});Q16=makeQuery(id+"F0.imprint","IMPRINT",FACE,{"disambiguationData":[TD([[makeQuery(id+"F0.imprint","IMPRINT",EDGE,{"disambiguationData":[TD([[subQ2,1.0]])],"derivedFrom":subQ1}),-1.0]])]});}
            var Q17;
            {var subQ0=sQuery(id+"F0.wireOp",EDGE,"E37.0");var subQ1=sQuery(id+"F0.wireOp",EDGE,"E24");var subQ2=makeQuery(id+"F0.imprint","INTERSECT",VERTEX,{"derivedFrom":[subQ1,subQ0]});Q17=makeQuery(id+"F0.imprint","IMPRINT",FACE,{"disambiguationData":[TD([[makeQuery(id+"F0.imprint","IMPRINT",EDGE,{"disambiguationData":[TD([[subQ2,1.0]])],"derivedFrom":subQ1}),-1.0]])]});}
            var Q18;
            {var subQ0=sQuery(id+"F0.wireOp",EDGE,"E35.0");var subQ1=sQuery(id+"F0.wireOp",EDGE,"E24");var subQ2=makeQuery(id+"F0.imprint","INTERSECT",VERTEX,{"derivedFrom":[subQ1,subQ0]});Q18=makeQuery(id+"F0.imprint","IMPRINT",FACE,{"disambiguationData":[TD([[makeQuery(id+"F0.imprint","IMPRINT",EDGE,{"disambiguationData":[TD([[subQ2,1.0]])],"derivedFrom":subQ1}),-1.0]])]});}
            var Q19;
            {var subQ0=sQuery(id+"F0.wireOp",EDGE,"E33.0");var subQ1=sQuery(id+"F0.wireOp",EDGE,"E24");var subQ2=makeQuery(id+"F0.imprint","INTERSECT",VERTEX,{"derivedFrom":[subQ1,subQ0]});Q19=makeQuery(id+"F0.imprint","IMPRINT",FACE,{"disambiguationData":[TD([[makeQuery(id+"F0.imprint","IMPRINT",EDGE,{"disambiguationData":[TD([[subQ2,1.0]])],"derivedFrom":subQ1}),-1.0]])]});}
            var Q20;
            {var subQ0=sQuery(id+"F0.wireOp",EDGE,"E31.0");var subQ1=sQuery(id+"F0.wireOp",EDGE,"E24");var subQ2=makeQuery(id+"F0.imprint","INTERSECT",VERTEX,{"derivedFrom":[subQ1,subQ0]});Q20=makeQuery(id+"F0.imprint","IMPRINT",FACE,{"disambiguationData":[TD([[makeQuery(id+"F0.imprint","IMPRINT",EDGE,{"disambiguationData":[TD([[subQ2,1.0]])],"derivedFrom":subQ1}),-1.0]])]});}
            var Q21;
            {var subQ0=sQuery(id+"F0.wireOp",EDGE,"E32.MirrorCS");var subQ1=sQuery(id+"F0.wireOp",EDGE,"E25");var subQ2=makeQuery(id+"F0.imprint","INTERSECT",VERTEX,{"derivedFrom":[subQ1,subQ0]});Q21=makeQuery(id+"F0.imprint","IMPRINT",FACE,{"disambiguationData":[TD([[makeQuery(id+"F0.imprint","IMPRINT",EDGE,{"disambiguationData":[TD([[subQ2,-1.0]])],"derivedFrom":subQ1}),-1.0]])]});}
            var Q22;
            {var subQ0=sQuery(id+"F0.wireOp",EDGE,"E34.MirrorCS");var subQ1=sQuery(id+"F0.wireOp",EDGE,"E25");var subQ2=makeQuery(id+"F0.imprint","INTERSECT",VERTEX,{"derivedFrom":[subQ1,subQ0]});Q22=makeQuery(id+"F0.imprint","IMPRINT",FACE,{"disambiguationData":[TD([[makeQuery(id+"F0.imprint","IMPRINT",EDGE,{"disambiguationData":[TD([[subQ2,-1.0]])],"derivedFrom":subQ1}),-1.0]])]});}
            var Q23;
            {var subQ0=sQuery(id+"F0.wireOp",EDGE,"E36.MirrorCS");var subQ1=sQuery(id+"F0.wireOp",EDGE,"E25");var subQ2=makeQuery(id+"F0.imprint","INTERSECT",VERTEX,{"derivedFrom":[subQ1,subQ0]});Q23=makeQuery(id+"F0.imprint","IMPRINT",FACE,{"disambiguationData":[TD([[makeQuery(id+"F0.imprint","IMPRINT",EDGE,{"disambiguationData":[TD([[subQ2,-1.0]])],"derivedFrom":subQ1}),-1.0]])]});}
            var Q24;
            {var subQ0=sQuery(id+"F0.wireOp",EDGE,"E38.0");var subQ1=sQuery(id+"F0.wireOp",EDGE,"E25");var subQ2=makeQuery(id+"F0.imprint","INTERSECT",VERTEX,{"derivedFrom":[subQ1,subQ0]});Q24=makeQuery(id+"F0.imprint","IMPRINT",FACE,{"disambiguationData":[TD([[makeQuery(id+"F0.imprint","IMPRINT",EDGE,{"disambiguationData":[TD([[subQ2,-1.0]])],"derivedFrom":subQ1}),-1.0]])]});}
            var Q25;
            {var subQ0=sQuery(id+"F0.wireOp",EDGE,"E40.0");var subQ1=sQuery(id+"F0.wireOp",EDGE,"E25");var subQ2=makeQuery(id+"F0.imprint","INTERSECT",VERTEX,{"derivedFrom":[subQ1,subQ0]});Q25=makeQuery(id+"F0.imprint","IMPRINT",FACE,{"disambiguationData":[TD([[makeQuery(id+"F0.imprint","IMPRINT",EDGE,{"disambiguationData":[TD([[subQ2,-1.0]])],"derivedFrom":subQ1}),-1.0]])]});}
            var Q26;
            {var subQ0=sQuery(id+"F0.wireOp",EDGE,"E44.0");var subQ1=sQuery(id+"F0.wireOp",EDGE,"E25");var subQ2=makeQuery(id+"F0.imprint","INTERSECT",VERTEX,{"derivedFrom":[subQ1,subQ0]});Q26=makeQuery(id+"F0.imprint","IMPRINT",FACE,{"disambiguationData":[TD([[makeQuery(id+"F0.imprint","IMPRINT",EDGE,{"disambiguationData":[TD([[subQ2,-1.0]])],"derivedFrom":subQ1}),-1.0]])]});}
            var Q27;
            {var subQ0=sQuery(id+"F0.wireOp",EDGE,"E42.0");var subQ1=sQuery(id+"F0.wireOp",EDGE,"E25");var subQ2=makeQuery(id+"F0.imprint","INTERSECT",VERTEX,{"derivedFrom":[subQ1,subQ0]});Q27=makeQuery(id+"F0.imprint","IMPRINT",FACE,{"disambiguationData":[TD([[makeQuery(id+"F0.imprint","IMPRINT",EDGE,{"disambiguationData":[TD([[subQ2,-1.0]])],"derivedFrom":subQ1}),-1.0]])]});}
            var Q28;
            {var subQ0=sQuery(id+"F0.wireOp",EDGE,"E26");var subQ1=sQuery(id+"F0.wireOp",EDGE,"E20.top");var subQ2=makeQuery(id+"F0.imprint","INTERSECT",VERTEX,{"disambiguationData":[OD(1.0)],"derivedFrom":[subQ1,subQ0]});Q28=makeQuery(id+"F0.imprint","IMPRINT",FACE,{"disambiguationData":[TD([[makeQuery(id+"F0.imprint","IMPRINT",EDGE,{"disambiguationData":[TD([[subQ2,1.0]])],"derivedFrom":subQ1}),1.0]])]});}
            var Q29;
            {var subQ0=sQuery(id+"F0.wireOp",EDGE,"E41.0");var subQ1=sQuery(id+"F0.wireOp",EDGE,"E26");var subQ2=makeQuery(id+"F0.imprint","INTERSECT",VERTEX,{"derivedFrom":[subQ1,subQ0]});Q29=makeQuery(id+"F0.imprint","IMPRINT",FACE,{"disambiguationData":[TD([[makeQuery(id+"F0.imprint","IMPRINT",EDGE,{"disambiguationData":[TD([[subQ2,1.0]])],"derivedFrom":subQ1}),-1.0]])]});}
            var Q30;
            {var subQ0=sQuery(id+"F0.wireOp",EDGE,"E42.0");var subQ1=sQuery(id+"F0.wireOp",EDGE,"E26");var subQ2=makeQuery(id+"F0.imprint","INTERSECT",VERTEX,{"derivedFrom":[subQ1,subQ0]});Q30=makeQuery(id+"F0.imprint","IMPRINT",FACE,{"disambiguationData":[TD([[makeQuery(id+"F0.imprint","IMPRINT",EDGE,{"disambiguationData":[TD([[subQ2,1.0]])],"derivedFrom":subQ1}),-1.0]])]});}
            var Q31;
            {var subQ0=sQuery(id+"F0.wireOp",EDGE,"E43.0");var subQ1=sQuery(id+"F0.wireOp",EDGE,"E26");var subQ2=makeQuery(id+"F0.imprint","INTERSECT",VERTEX,{"derivedFrom":[subQ1,subQ0]});Q31=makeQuery(id+"F0.imprint","IMPRINT",FACE,{"disambiguationData":[TD([[makeQuery(id+"F0.imprint","IMPRINT",EDGE,{"disambiguationData":[TD([[subQ2,1.0]])],"derivedFrom":subQ1}),-1.0]])]});}
            var Q32;
            {var subQ0=sQuery(id+"F0.wireOp",EDGE,"E39.0");var subQ1=sQuery(id+"F0.wireOp",EDGE,"E26");var subQ2=makeQuery(id+"F0.imprint","INTERSECT",VERTEX,{"derivedFrom":[subQ1,subQ0]});Q32=makeQuery(id+"F0.imprint","IMPRINT",FACE,{"disambiguationData":[TD([[makeQuery(id+"F0.imprint","IMPRINT",EDGE,{"disambiguationData":[TD([[subQ2,-1.0]])],"derivedFrom":subQ1}),-1.0]])]});}
            var Q33;
            {var subQ0=sQuery(id+"F0.wireOp",EDGE,"E39.0");var subQ1=sQuery(id+"F0.wireOp",EDGE,"E26");var subQ2=makeQuery(id+"F0.imprint","INTERSECT",VERTEX,{"derivedFrom":[subQ1,subQ0]});Q33=makeQuery(id+"F0.imprint","IMPRINT",FACE,{"disambiguationData":[TD([[makeQuery(id+"F0.imprint","IMPRINT",EDGE,{"disambiguationData":[TD([[subQ2,1.0]])],"derivedFrom":subQ1}),-1.0]])]});}
            var Q34;
            {var subQ0=sQuery(id+"F0.wireOp",EDGE,"E37.0");var subQ1=sQuery(id+"F0.wireOp",EDGE,"E26");var subQ2=makeQuery(id+"F0.imprint","INTERSECT",VERTEX,{"derivedFrom":[subQ1,subQ0]});Q34=makeQuery(id+"F0.imprint","IMPRINT",FACE,{"disambiguationData":[TD([[makeQuery(id+"F0.imprint","IMPRINT",EDGE,{"disambiguationData":[TD([[subQ2,-1.0]])],"derivedFrom":subQ1}),-1.0]])]});}
            var Q35;
            {var subQ0=sQuery(id+"F0.wireOp",EDGE,"E37.0");var subQ1=sQuery(id+"F0.wireOp",EDGE,"E26");var subQ2=makeQuery(id+"F0.imprint","INTERSECT",VERTEX,{"derivedFrom":[subQ1,subQ0]});Q35=makeQuery(id+"F0.imprint","IMPRINT",FACE,{"disambiguationData":[TD([[makeQuery(id+"F0.imprint","IMPRINT",EDGE,{"disambiguationData":[TD([[subQ2,1.0]])],"derivedFrom":subQ1}),-1.0]])]});}
            var Q36;
            {var subQ0=sQuery(id+"F0.wireOp",EDGE,"E35.0");var subQ1=sQuery(id+"F0.wireOp",EDGE,"E26");var subQ2=makeQuery(id+"F0.imprint","INTERSECT",VERTEX,{"derivedFrom":[subQ1,subQ0]});Q36=makeQuery(id+"F0.imprint","IMPRINT",FACE,{"disambiguationData":[TD([[makeQuery(id+"F0.imprint","IMPRINT",EDGE,{"disambiguationData":[TD([[subQ2,-1.0]])],"derivedFrom":subQ1}),-1.0]])]});}
            var Q37;
            {var subQ0=sQuery(id+"F0.wireOp",EDGE,"E35.0");var subQ1=sQuery(id+"F0.wireOp",EDGE,"E26");var subQ2=makeQuery(id+"F0.imprint","INTERSECT",VERTEX,{"derivedFrom":[subQ1,subQ0]});Q37=makeQuery(id+"F0.imprint","IMPRINT",FACE,{"disambiguationData":[TD([[makeQuery(id+"F0.imprint","IMPRINT",EDGE,{"disambiguationData":[TD([[subQ2,1.0]])],"derivedFrom":subQ1}),-1.0]])]});}
            var Q38;
            {var subQ0=sQuery(id+"F0.wireOp",EDGE,"E33.0");var subQ1=sQuery(id+"F0.wireOp",EDGE,"E26");var subQ2=makeQuery(id+"F0.imprint","INTERSECT",VERTEX,{"derivedFrom":[subQ1,subQ0]});Q38=makeQuery(id+"F0.imprint","IMPRINT",FACE,{"disambiguationData":[TD([[makeQuery(id+"F0.imprint","IMPRINT",EDGE,{"disambiguationData":[TD([[subQ2,-1.0]])],"derivedFrom":subQ1}),-1.0]])]});}
            var Q39;
            {var subQ0=sQuery(id+"F0.wireOp",EDGE,"E33.0");var subQ1=sQuery(id+"F0.wireOp",EDGE,"E26");var subQ2=makeQuery(id+"F0.imprint","INTERSECT",VERTEX,{"derivedFrom":[subQ1,subQ0]});Q39=makeQuery(id+"F0.imprint","IMPRINT",FACE,{"disambiguationData":[TD([[makeQuery(id+"F0.imprint","IMPRINT",EDGE,{"disambiguationData":[TD([[subQ2,1.0]])],"derivedFrom":subQ1}),-1.0]])]});}
            var Q40;
            {var subQ0=sQuery(id+"F0.wireOp",EDGE,"E31.0");var subQ1=sQuery(id+"F0.wireOp",EDGE,"E26");var subQ2=makeQuery(id+"F0.imprint","INTERSECT",VERTEX,{"derivedFrom":[subQ1,subQ0]});Q40=makeQuery(id+"F0.imprint","IMPRINT",FACE,{"disambiguationData":[TD([[makeQuery(id+"F0.imprint","IMPRINT",EDGE,{"disambiguationData":[TD([[subQ2,-1.0]])],"derivedFrom":subQ1}),-1.0]])]});}
            var Q41;
            {var subQ0=sQuery(id+"F0.wireOp",EDGE,"E31.0");var subQ1=sQuery(id+"F0.wireOp",EDGE,"E26");var subQ2=makeQuery(id+"F0.imprint","INTERSECT",VERTEX,{"derivedFrom":[subQ1,subQ0]});Q41=makeQuery(id+"F0.imprint","IMPRINT",FACE,{"disambiguationData":[TD([[makeQuery(id+"F0.imprint","IMPRINT",EDGE,{"disambiguationData":[TD([[subQ2,1.0]])],"derivedFrom":subQ1}),-1.0]])]});}
            var Q42;
            {var subQ0=sQuery(id+"F0.wireOp",EDGE,"E26");var subQ1=sQuery(id+"F0.wireOp",EDGE,"E20.top");var subQ2=makeQuery(id+"F0.imprint","INTERSECT",VERTEX,{"disambiguationData":[OD(0.0)],"derivedFrom":[subQ1,subQ0]});Q42=makeQuery(id+"F0.imprint","IMPRINT",FACE,{"disambiguationData":[TD([[makeQuery(id+"F0.imprint","IMPRINT",EDGE,{"disambiguationData":[TD([[subQ2,-1.0]])],"derivedFrom":subQ1}),1.0]])]});}
            var Q43;
            {var subQ10=sQuery(id+"F0.wireOp",EDGE,"E28");Q43=makeQuery(id+"F0.imprint","IMPRINT",FACE,{"disambiguationData":[TD([[makeQuery(id+"F0.imprint","IMPRINT",EDGE,{"derivedFrom":subQ10}),1.0]])]});}
            var Q44;
            {var subQ0=sQuery(id+"F0.wireOp",EDGE,"E34.MirrorCS");var subQ3=sQuery(id+"F0.wireOp",EDGE,"E27");var subQ4=makeQuery(id+"F0.imprint","INTERSECT",VERTEX,{"derivedFrom":[subQ3,subQ0]});Q44=makeQuery(id+"F0.imprint","IMPRINT",FACE,{"disambiguationData":[TD([[makeQuery(id+"F0.imprint","IMPRINT",EDGE,{"disambiguationData":[TD([[subQ4,-1.0]])],"derivedFrom":subQ3}),-1.0]])]});}
            var Q45;
            {var subQ0=sQuery(id+"F0.wireOp",EDGE,"E38.0");var subQ3=sQuery(id+"F0.wireOp",EDGE,"E27");var subQ4=makeQuery(id+"F0.imprint","INTERSECT",VERTEX,{"derivedFrom":[subQ3,subQ0]});Q45=makeQuery(id+"F0.imprint","IMPRINT",FACE,{"disambiguationData":[TD([[makeQuery(id+"F0.imprint","IMPRINT",EDGE,{"disambiguationData":[TD([[subQ4,-1.0]])],"derivedFrom":subQ3}),-1.0]])]});}
            var Q46;
            {var subQ0=sQuery(id+"F0.wireOp",EDGE,"E33.0");var subQ1=sQuery(id+"F0.wireOp",EDGE,"E24");var subQ2=makeQuery(id+"F0.imprint","INTERSECT",VERTEX,{"derivedFrom":[subQ1,subQ0]});Q46=makeQuery(id+"F0.imprint","IMPRINT",FACE,{"disambiguationData":[TD([[makeQuery(id+"F0.imprint","IMPRINT",EDGE,{"disambiguationData":[TD([[subQ2,-1.0]])],"derivedFrom":subQ1}),-1.0]])]});}
            extrude(context, id + "F2", {"entities" : qUnion([Q0, Q1, Q2, Q3, Q4, Q5, Q6, Q7, Q8, Q9, Q10, Q11, Q12, Q13, Q14, Q15, Q16, Q17, Q18, Q19, Q20, Q21, Q22, Q23, Q24, Q25, Q26, Q27, Q28, Q29, Q30, Q31, Q32, Q33, Q34, Q35, Q36, Q37, Q38, Q39, Q40, Q41, Q42, Q43, Q44, Q45, Q46]), "operationType" : NewBodyOperationType.ADD, "depth" : 1.5 * mm});
        }
        {
            var Q0;
            {var subQ26=sQuery(id+"F0.wireOp",EDGE,"E13.top");Q0=makeQuery(id+"F0.imprint","IMPRINT",FACE,{"disambiguationData":[TD([[makeQuery(id+"F0.imprint","IMPRINT",EDGE,{"derivedFrom":subQ26}),-1.0]])]});}
            extrude(context, id + "F3", {"entities" : qUnion([Q0]), "operationType" : NewBodyOperationType.ADD, "depth" : 2 * mm});
        }
        {
            var Q0;
            Q0=makeQuery(id+"F3.opExtrude","CAP_EDGE",EDGE,{"disambiguationData":[OSD([sQuery(id+"F0.wireOp",EDGE,"E18.4.5.4")])],"isStart":false});
            var Q1;
            Q1=makeQuery(id+"F3.opExtrude","CAP_EDGE",EDGE,{"disambiguationData":[OSD([sQuery(id+"F0.wireOp",EDGE,"E18.4.5.3")])],"isStart":false});
            var Q2;
            Q2=makeQuery(id+"F3.opExtrude","CAP_EDGE",EDGE,{"disambiguationData":[OSD([sQuery(id+"F0.wireOp",EDGE,"E18.3.5.4")])],"isStart":false});
            var Q3;
            Q3=makeQuery(id+"F3.opExtrude","CAP_EDGE",EDGE,{"disambiguationData":[OSD([sQuery(id+"F0.wireOp",EDGE,"E18.3.5.3")])],"isStart":false});
            var Q4;
            Q4=makeQuery(id+"F3.opExtrude","CAP_EDGE",EDGE,{"disambiguationData":[OSD([sQuery(id+"F0.wireOp",EDGE,"E18.2.5.4")])],"isStart":false});
            var Q5;
            Q5=makeQuery(id+"F3.opExtrude","CAP_EDGE",EDGE,{"disambiguationData":[OSD([sQuery(id+"F0.wireOp",EDGE,"E18.2.5.3")])],"isStart":false});
            var Q6;
            Q6=makeQuery(id+"F3.opExtrude","CAP_EDGE",EDGE,{"disambiguationData":[OSD([sQuery(id+"F0.wireOp",EDGE,"E18.1.5.4")])],"isStart":false});
            var Q7;
            Q7=makeQuery(id+"F3.opExtrude","CAP_EDGE",EDGE,{"disambiguationData":[OSD([sQuery(id+"F0.wireOp",EDGE,"E18.1.5.3")])],"isStart":false});
            var Q8;
            Q8=makeQuery(id+"F3.opExtrude","CAP_EDGE",EDGE,{"disambiguationData":[OSD([sQuery(id+"F0.wireOp",EDGE,"E18.1.4.1")])],"isStart":false});
            var Q9;
            Q9=makeQuery(id+"F3.opExtrude","CAP_EDGE",EDGE,{"disambiguationData":[OSD([sQuery(id+"F0.wireOp",EDGE,"E18.1.4.2")])],"isStart":false});
            var Q10;
            Q10=makeQuery(id+"F3.opExtrude","CAP_EDGE",EDGE,{"disambiguationData":[OSD([sQuery(id+"F0.wireOp",EDGE,"E18.1.4.3")])],"isStart":false});
            var Q11;
            Q11=makeQuery(id+"F3.opExtrude","CAP_EDGE",EDGE,{"disambiguationData":[OSD([sQuery(id+"F0.wireOp",EDGE,"E18.1.4.4")])],"isStart":false});
            var Q12;
            Q12=makeQuery(id+"F3.opExtrude","CAP_EDGE",EDGE,{"disambiguationData":[OSD([sQuery(id+"F0.wireOp",EDGE,"E18.2.4.2")])],"isStart":false});
            var Q13;
            Q13=makeQuery(id+"F3.opExtrude","CAP_EDGE",EDGE,{"disambiguationData":[OSD([sQuery(id+"F0.wireOp",EDGE,"E18.2.4.1")])],"isStart":false});
            var Q14;
            Q14=makeQuery(id+"F3.opExtrude","CAP_EDGE",EDGE,{"disambiguationData":[OSD([sQuery(id+"F0.wireOp",EDGE,"E18.3.4.2")])],"isStart":false});
            var Q15;
            Q15=makeQuery(id+"F3.opExtrude","CAP_EDGE",EDGE,{"disambiguationData":[OSD([sQuery(id+"F0.wireOp",EDGE,"E18.3.4.1")])],"isStart":false});
            var Q16;
            Q16=makeQuery(id+"F3.opExtrude","CAP_EDGE",EDGE,{"disambiguationData":[OSD([sQuery(id+"F0.wireOp",EDGE,"E18.4.4.1")])],"isStart":false});
            var Q17;
            Q17=makeQuery(id+"F3.opExtrude","CAP_EDGE",EDGE,{"disambiguationData":[OSD([sQuery(id+"F0.wireOp",EDGE,"E18.4.4.2")])],"isStart":false});
            var Q18;
            Q18=makeQuery(id+"F3.opExtrude","CAP_EDGE",EDGE,{"disambiguationData":[OSD([sQuery(id+"F0.wireOp",EDGE,"E18.5.4.1")])],"isStart":false});
            var Q19;
            Q19=makeQuery(id+"F3.opExtrude","CAP_EDGE",EDGE,{"disambiguationData":[OSD([sQuery(id+"F0.wireOp",EDGE,"E18.5.4.2")])],"isStart":false});
            var Q20;
            Q20=makeQuery(id+"F3.opExtrude","CAP_EDGE",EDGE,{"disambiguationData":[OSD([sQuery(id+"F0.wireOp",EDGE,"E18.4.4.4")])],"isStart":false});
            var Q21;
            Q21=makeQuery(id+"F3.opExtrude","CAP_EDGE",EDGE,{"disambiguationData":[OSD([sQuery(id+"F0.wireOp",EDGE,"E18.4.4.3")])],"isStart":false});
            var Q22;
            Q22=makeQuery(id+"F3.opExtrude","CAP_EDGE",EDGE,{"disambiguationData":[OSD([sQuery(id+"F0.wireOp",EDGE,"E18.4.3.4")])],"isStart":false});
            var Q23;
            Q23=makeQuery(id+"F3.opExtrude","CAP_EDGE",EDGE,{"disambiguationData":[OSD([sQuery(id+"F0.wireOp",EDGE,"E18.4.3.3")])],"isStart":false});
            var Q24;
            Q24=makeQuery(id+"F3.opExtrude","CAP_EDGE",EDGE,{"disambiguationData":[OSD([sQuery(id+"F0.wireOp",EDGE,"E18.3.3.4")])],"isStart":false});
            var Q25;
            Q25=makeQuery(id+"F3.opExtrude","CAP_EDGE",EDGE,{"disambiguationData":[OSD([sQuery(id+"F0.wireOp",EDGE,"E18.3.4.4")])],"isStart":false});
            var Q26;
            Q26=makeQuery(id+"F3.opExtrude","CAP_EDGE",EDGE,{"disambiguationData":[OSD([sQuery(id+"F0.wireOp",EDGE,"E18.3.4.3")])],"isStart":false});
            var Q27;
            Q27=makeQuery(id+"F3.opExtrude","CAP_EDGE",EDGE,{"disambiguationData":[OSD([sQuery(id+"F0.wireOp",EDGE,"E18.2.4.4")])],"isStart":false});
            var Q28;
            Q28=makeQuery(id+"F3.opExtrude","CAP_EDGE",EDGE,{"disambiguationData":[OSD([sQuery(id+"F0.wireOp",EDGE,"E18.2.4.3")])],"isStart":false});
            var Q29;
            Q29=makeQuery(id+"F3.opExtrude","CAP_EDGE",EDGE,{"disambiguationData":[OSD([sQuery(id+"F0.wireOp",EDGE,"E18.2.3.4")])],"isStart":false});
            var Q30;
            Q30=makeQuery(id+"F3.opExtrude","CAP_EDGE",EDGE,{"disambiguationData":[OSD([sQuery(id+"F0.wireOp",EDGE,"E18.2.3.3")])],"isStart":false});
            var Q31;
            Q31=makeQuery(id+"F3.opExtrude","CAP_EDGE",EDGE,{"disambiguationData":[OSD([sQuery(id+"F0.wireOp",EDGE,"E18.1.3.4")])],"isStart":false});
            var Q32;
            Q32=makeQuery(id+"F3.opExtrude","CAP_EDGE",EDGE,{"disambiguationData":[OSD([sQuery(id+"F0.wireOp",EDGE,"E18.1.3.3")])],"isStart":false});
            var Q33;
            Q33=makeQuery(id+"F3.opExtrude","CAP_EDGE",EDGE,{"disambiguationData":[OSD([sQuery(id+"F0.wireOp",EDGE,"E18.0.3.4")])],"isStart":false});
            var Q34;
            Q34=makeQuery(id+"F3.opExtrude","CAP_EDGE",EDGE,{"disambiguationData":[OSD([sQuery(id+"F0.wireOp",EDGE,"E18.0.3.3")])],"isStart":false});
            var Q35;
            Q35=makeQuery(id+"F3.opExtrude","CAP_EDGE",EDGE,{"disambiguationData":[OSD([sQuery(id+"F0.wireOp",EDGE,"E18.0.4.4")])],"isStart":false});
            var Q36;
            Q36=makeQuery(id+"F3.opExtrude","CAP_EDGE",EDGE,{"disambiguationData":[OSD([sQuery(id+"F0.wireOp",EDGE,"E18.0.4.3")])],"isStart":false});
            var Q37;
            Q37=makeQuery(id+"F3.opExtrude","CAP_EDGE",EDGE,{"disambiguationData":[OSD([sQuery(id+"F0.wireOp",EDGE,"E18.0.5.4")])],"isStart":false});
            var Q38;
            Q38=makeQuery(id+"F3.opExtrude","CAP_EDGE",EDGE,{"disambiguationData":[OSD([sQuery(id+"F0.wireOp",EDGE,"E18.0.5.3")])],"isStart":false});
            var Q39;
            Q39=makeQuery(id+"F3.opExtrude","CAP_EDGE",EDGE,{"disambiguationData":[OSD([sQuery(id+"F0.wireOp",EDGE,"E18.0.4.1")])],"isStart":false});
            var Q40;
            Q40=makeQuery(id+"F3.opExtrude","CAP_EDGE",EDGE,{"disambiguationData":[OSD([sQuery(id+"F0.wireOp",EDGE,"E18.0.4.2")])],"isStart":false});
            var Q41;
            Q41=makeQuery(id+"F3.opExtrude","CAP_EDGE",EDGE,{"disambiguationData":[OSD([sQuery(id+"F0.wireOp",EDGE,"E18.0.3.2")])],"isStart":false});
            var Q42;
            Q42=makeQuery(id+"F3.opExtrude","CAP_EDGE",EDGE,{"disambiguationData":[OSD([sQuery(id+"F0.wireOp",EDGE,"E18.0.3.1")])],"isStart":false});
            var Q43;
            Q43=makeQuery(id+"F3.opExtrude","CAP_EDGE",EDGE,{"disambiguationData":[OSD([sQuery(id+"F0.wireOp",EDGE,"E18.1.3.2")])],"isStart":false});
            var Q44;
            Q44=makeQuery(id+"F3.opExtrude","CAP_EDGE",EDGE,{"disambiguationData":[OSD([sQuery(id+"F0.wireOp",EDGE,"E18.1.3.1")])],"isStart":false});
            var Q45;
            Q45=makeQuery(id+"F3.opExtrude","CAP_EDGE",EDGE,{"disambiguationData":[OSD([sQuery(id+"F0.wireOp",EDGE,"E18.2.3.2")])],"isStart":false});
            var Q46;
            Q46=makeQuery(id+"F3.opExtrude","CAP_EDGE",EDGE,{"disambiguationData":[OSD([sQuery(id+"F0.wireOp",EDGE,"E18.2.3.1")])],"isStart":false});
            var Q47;
            Q47=makeQuery(id+"F3.opExtrude","CAP_EDGE",EDGE,{"disambiguationData":[OSD([sQuery(id+"F0.wireOp",EDGE,"E18.3.3.2")])],"isStart":false});
            var Q48;
            Q48=makeQuery(id+"F3.opExtrude","CAP_EDGE",EDGE,{"disambiguationData":[OSD([sQuery(id+"F0.wireOp",EDGE,"E18.3.3.1")])],"isStart":false});
            var Q49;
            Q49=makeQuery(id+"F3.opExtrude","CAP_EDGE",EDGE,{"disambiguationData":[OSD([sQuery(id+"F0.wireOp",EDGE,"E18.4.3.2")])],"isStart":false});
            var Q50;
            Q50=makeQuery(id+"F3.opExtrude","CAP_EDGE",EDGE,{"disambiguationData":[OSD([sQuery(id+"F0.wireOp",EDGE,"E18.4.3.1")])],"isStart":false});
            var Q51;
            Q51=makeQuery(id+"F3.opExtrude","CAP_EDGE",EDGE,{"disambiguationData":[OSD([sQuery(id+"F0.wireOp",EDGE,"E18.3.3.3")])],"isStart":false});
            var Q52;
            Q52=makeQuery(id+"F3.opExtrude","CAP_EDGE",EDGE,{"disambiguationData":[OSD([sQuery(id+"F0.wireOp",EDGE,"E18.5.3.1")])],"isStart":false});
            var Q53;
            Q53=makeQuery(id+"F3.opExtrude","CAP_EDGE",EDGE,{"disambiguationData":[OSD([sQuery(id+"F0.wireOp",EDGE,"E18.5.3.2")])],"isStart":false});
            var Q54;
            Q54=makeQuery(id+"F3.opExtrude","CAP_EDGE",EDGE,{"disambiguationData":[OSD([sQuery(id+"F0.wireOp",EDGE,"E18.5.2.1")])],"isStart":false});
            var Q55;
            Q55=makeQuery(id+"F3.opExtrude","CAP_EDGE",EDGE,{"disambiguationData":[OSD([sQuery(id+"F0.wireOp",EDGE,"E18.5.2.2")])],"isStart":false});
            var Q56;
            Q56=makeQuery(id+"F3.opExtrude","CAP_EDGE",EDGE,{"disambiguationData":[OSD([sQuery(id+"F0.wireOp",EDGE,"E18.4.2.4")])],"isStart":false});
            var Q57;
            Q57=makeQuery(id+"F3.opExtrude","CAP_EDGE",EDGE,{"disambiguationData":[OSD([sQuery(id+"F0.wireOp",EDGE,"E18.4.2.3")])],"isStart":false});
            var Q58;
            Q58=makeQuery(id+"F3.opExtrude","CAP_EDGE",EDGE,{"disambiguationData":[OSD([sQuery(id+"F0.wireOp",EDGE,"E18.4.2.1")])],"isStart":false});
            var Q59;
            Q59=makeQuery(id+"F3.opExtrude","CAP_EDGE",EDGE,{"disambiguationData":[OSD([sQuery(id+"F0.wireOp",EDGE,"E18.4.2.2")])],"isStart":false});
            var Q60;
            Q60=makeQuery(id+"F3.opExtrude","CAP_EDGE",EDGE,{"disambiguationData":[OSD([sQuery(id+"F0.wireOp",EDGE,"E18.3.2.1")])],"isStart":false});
            var Q61;
            Q61=makeQuery(id+"F3.opExtrude","CAP_EDGE",EDGE,{"disambiguationData":[OSD([sQuery(id+"F0.wireOp",EDGE,"E18.3.2.2")])],"isStart":false});
            var Q62;
            Q62=makeQuery(id+"F3.opExtrude","CAP_EDGE",EDGE,{"disambiguationData":[OSD([sQuery(id+"F0.wireOp",EDGE,"E18.2.2.1")])],"isStart":false});
            var Q63;
            Q63=makeQuery(id+"F3.opExtrude","CAP_EDGE",EDGE,{"disambiguationData":[OSD([sQuery(id+"F0.wireOp",EDGE,"E18.2.2.2")])],"isStart":false});
            var Q64;
            Q64=makeQuery(id+"F3.opExtrude","CAP_EDGE",EDGE,{"disambiguationData":[OSD([sQuery(id+"F0.wireOp",EDGE,"E18.1.2.1")])],"isStart":false});
            var Q65;
            Q65=makeQuery(id+"F3.opExtrude","CAP_EDGE",EDGE,{"disambiguationData":[OSD([sQuery(id+"F0.wireOp",EDGE,"E18.1.2.2")])],"isStart":false});
            var Q66;
            Q66=makeQuery(id+"F3.opExtrude","CAP_EDGE",EDGE,{"disambiguationData":[OSD([sQuery(id+"F0.wireOp",EDGE,"E18.0.2.1")])],"isStart":false});
            var Q67;
            Q67=makeQuery(id+"F3.opExtrude","CAP_EDGE",EDGE,{"disambiguationData":[OSD([sQuery(id+"F0.wireOp",EDGE,"E18.0.2.2")])],"isStart":false});
            var Q68;
            Q68=makeQuery(id+"F3.opExtrude","CAP_EDGE",EDGE,{"disambiguationData":[OSD([sQuery(id+"F0.wireOp",EDGE,"E18.0.2.3")])],"isStart":false});
            var Q69;
            Q69=makeQuery(id+"F3.opExtrude","CAP_EDGE",EDGE,{"disambiguationData":[OSD([sQuery(id+"F0.wireOp",EDGE,"E18.0.2.4")])],"isStart":false});
            var Q70;
            Q70=makeQuery(id+"F3.opExtrude","CAP_EDGE",EDGE,{"disambiguationData":[OSD([sQuery(id+"F0.wireOp",EDGE,"E18.0.1.1")])],"isStart":false});
            var Q71;
            Q71=makeQuery(id+"F3.opExtrude","CAP_EDGE",EDGE,{"disambiguationData":[OSD([sQuery(id+"F0.wireOp",EDGE,"E18.0.1.2")])],"isStart":false});
            var Q72;
            Q72=makeQuery(id+"F3.opExtrude","CAP_EDGE",EDGE,{"disambiguationData":[OSD([sQuery(id+"F0.wireOp",EDGE,"E15.top")])],"isStart":false});
            var Q73;
            Q73=makeQuery(id+"F3.opExtrude","CAP_EDGE",EDGE,{"disambiguationData":[OSD([sQuery(id+"F0.wireOp",EDGE,"E13.top")])],"isStart":false});
            var Q74;
            Q74=makeQuery(id+"F3.opExtrude","CAP_EDGE",EDGE,{"disambiguationData":[OSD([sQuery(id+"F0.wireOp",EDGE,"E18.0.1.3")])],"isStart":false});
            var Q75;
            Q75=makeQuery(id+"F3.opExtrude","CAP_EDGE",EDGE,{"disambiguationData":[OSD([sQuery(id+"F0.wireOp",EDGE,"E18.0.1.4")])],"isStart":false});
            var Q76;
            Q76=makeQuery(id+"F3.opExtrude","CAP_EDGE",EDGE,{"disambiguationData":[OSD([sQuery(id+"F0.wireOp",EDGE,"E13.right")])],"isStart":false});
            var Q77;
            Q77=makeQuery(id+"F3.opExtrude","CAP_EDGE",EDGE,{"disambiguationData":[OSD([sQuery(id+"F0.wireOp",EDGE,"E14.right")])],"isStart":false});
            var Q78;
            Q78=makeQuery(id+"F3.opExtrude","CAP_EDGE",EDGE,{"disambiguationData":[OSD([sQuery(id+"F0.wireOp",EDGE,"E18.1.0.2")])],"isStart":false});
            var Q79;
            Q79=makeQuery(id+"F3.opExtrude","CAP_EDGE",EDGE,{"disambiguationData":[OSD([sQuery(id+"F0.wireOp",EDGE,"E18.1.0.1")])],"isStart":false});
            var Q80;
            Q80=makeQuery(id+"F3.opExtrude","CAP_EDGE",EDGE,{"disambiguationData":[OSD([sQuery(id+"F0.wireOp",EDGE,"E18.1.1.2")])],"isStart":false});
            var Q81;
            Q81=makeQuery(id+"F3.opExtrude","CAP_EDGE",EDGE,{"disambiguationData":[OSD([sQuery(id+"F0.wireOp",EDGE,"E18.1.1.1")])],"isStart":false});
            var Q82;
            Q82=makeQuery(id+"F3.opExtrude","CAP_EDGE",EDGE,{"disambiguationData":[OSD([sQuery(id+"F0.wireOp",EDGE,"E18.1.0.3")])],"isStart":false});
            var Q83;
            Q83=makeQuery(id+"F3.opExtrude","CAP_EDGE",EDGE,{"disambiguationData":[OSD([sQuery(id+"F0.wireOp",EDGE,"E18.1.0.4")])],"isStart":false});
            var Q84;
            Q84=makeQuery(id+"F3.opExtrude","CAP_EDGE",EDGE,{"disambiguationData":[OSD([sQuery(id+"F0.wireOp",EDGE,"E18.1.1.4")])],"isStart":false});
            var Q85;
            Q85=makeQuery(id+"F3.opExtrude","CAP_EDGE",EDGE,{"disambiguationData":[OSD([sQuery(id+"F0.wireOp",EDGE,"E18.1.1.3")])],"isStart":false});
            var Q86;
            Q86=makeQuery(id+"F3.opExtrude","CAP_EDGE",EDGE,{"disambiguationData":[OSD([sQuery(id+"F0.wireOp",EDGE,"E18.1.2.4")])],"isStart":false});
            var Q87;
            Q87=makeQuery(id+"F3.opExtrude","CAP_EDGE",EDGE,{"disambiguationData":[OSD([sQuery(id+"F0.wireOp",EDGE,"E18.1.2.3")])],"isStart":false});
            var Q88;
            Q88=makeQuery(id+"F3.opExtrude","CAP_EDGE",EDGE,{"disambiguationData":[OSD([sQuery(id+"F0.wireOp",EDGE,"E18.2.1.1")])],"isStart":false});
            var Q89;
            Q89=makeQuery(id+"F3.opExtrude","CAP_EDGE",EDGE,{"disambiguationData":[OSD([sQuery(id+"F0.wireOp",EDGE,"E18.2.1.2")])],"isStart":false});
            var Q90;
            Q90=makeQuery(id+"F3.opExtrude","CAP_EDGE",EDGE,{"disambiguationData":[OSD([sQuery(id+"F0.wireOp",EDGE,"E18.2.0.1")])],"isStart":false});
            var Q91;
            Q91=makeQuery(id+"F3.opExtrude","CAP_EDGE",EDGE,{"disambiguationData":[OSD([sQuery(id+"F0.wireOp",EDGE,"E18.2.0.2")])],"isStart":false});
            var Q92;
            Q92=makeQuery(id+"F3.opExtrude","CAP_EDGE",EDGE,{"disambiguationData":[OSD([sQuery(id+"F0.wireOp",EDGE,"E18.2.2.3")])],"isStart":false});
            var Q93;
            Q93=makeQuery(id+"F3.opExtrude","CAP_EDGE",EDGE,{"disambiguationData":[OSD([sQuery(id+"F0.wireOp",EDGE,"E18.2.2.4")])],"isStart":false});
            var Q94;
            Q94=makeQuery(id+"F3.opExtrude","CAP_EDGE",EDGE,{"disambiguationData":[OSD([sQuery(id+"F0.wireOp",EDGE,"E18.2.1.4")])],"isStart":false});
            var Q95;
            Q95=makeQuery(id+"F3.opExtrude","CAP_EDGE",EDGE,{"disambiguationData":[OSD([sQuery(id+"F0.wireOp",EDGE,"E18.2.1.3")])],"isStart":false});
            var Q96;
            Q96=makeQuery(id+"F3.opExtrude","CAP_EDGE",EDGE,{"disambiguationData":[OSD([sQuery(id+"F0.wireOp",EDGE,"E18.2.0.4")])],"isStart":false});
            var Q97;
            Q97=makeQuery(id+"F3.opExtrude","CAP_EDGE",EDGE,{"disambiguationData":[OSD([sQuery(id+"F0.wireOp",EDGE,"E18.2.0.3")])],"isStart":false});
            var Q98;
            Q98=makeQuery(id+"F3.opExtrude","CAP_EDGE",EDGE,{"disambiguationData":[OSD([sQuery(id+"F0.wireOp",EDGE,"E18.3.0.2")])],"isStart":false});
            var Q99;
            Q99=makeQuery(id+"F3.opExtrude","CAP_EDGE",EDGE,{"disambiguationData":[OSD([sQuery(id+"F0.wireOp",EDGE,"E18.3.0.1")])],"isStart":false});
            var Q100;
            Q100=makeQuery(id+"F3.opExtrude","CAP_EDGE",EDGE,{"disambiguationData":[OSD([sQuery(id+"F0.wireOp",EDGE,"E18.3.1.2")])],"isStart":false});
            var Q101;
            Q101=makeQuery(id+"F3.opExtrude","CAP_EDGE",EDGE,{"disambiguationData":[OSD([sQuery(id+"F0.wireOp",EDGE,"E18.3.1.1")])],"isStart":false});
            var Q102;
            Q102=makeQuery(id+"F3.opExtrude","CAP_EDGE",EDGE,{"disambiguationData":[OSD([sQuery(id+"F0.wireOp",EDGE,"E18.3.0.3")])],"isStart":false});
            var Q103;
            Q103=makeQuery(id+"F3.opExtrude","CAP_EDGE",EDGE,{"disambiguationData":[OSD([sQuery(id+"F0.wireOp",EDGE,"E18.3.0.4")])],"isStart":false});
            var Q104;
            Q104=makeQuery(id+"F3.opExtrude","CAP_EDGE",EDGE,{"disambiguationData":[OSD([sQuery(id+"F0.wireOp",EDGE,"E18.3.1.4")])],"isStart":false});
            var Q105;
            Q105=makeQuery(id+"F3.opExtrude","CAP_EDGE",EDGE,{"disambiguationData":[OSD([sQuery(id+"F0.wireOp",EDGE,"E18.3.1.3")])],"isStart":false});
            var Q106;
            Q106=makeQuery(id+"F3.opExtrude","CAP_EDGE",EDGE,{"disambiguationData":[OSD([sQuery(id+"F0.wireOp",EDGE,"E18.3.2.3")])],"isStart":false});
            var Q107;
            Q107=makeQuery(id+"F3.opExtrude","CAP_EDGE",EDGE,{"disambiguationData":[OSD([sQuery(id+"F0.wireOp",EDGE,"E18.3.2.4")])],"isStart":false});
            var Q108;
            Q108=makeQuery(id+"F3.opExtrude","CAP_EDGE",EDGE,{"disambiguationData":[OSD([sQuery(id+"F0.wireOp",EDGE,"E18.4.1.2")])],"isStart":false});
            var Q109;
            Q109=makeQuery(id+"F3.opExtrude","CAP_EDGE",EDGE,{"disambiguationData":[OSD([sQuery(id+"F0.wireOp",EDGE,"E18.4.1.1")])],"isStart":false});
            var Q110;
            Q110=makeQuery(id+"F3.opExtrude","CAP_EDGE",EDGE,{"disambiguationData":[OSD([sQuery(id+"F0.wireOp",EDGE,"E18.4.1.4")])],"isStart":false});
            var Q111;
            Q111=makeQuery(id+"F3.opExtrude","CAP_EDGE",EDGE,{"disambiguationData":[OSD([sQuery(id+"F0.wireOp",EDGE,"E18.4.1.3")])],"isStart":false});
            var Q112;
            Q112=makeQuery(id+"F3.opExtrude","CAP_EDGE",EDGE,{"disambiguationData":[OSD([sQuery(id+"F0.wireOp",EDGE,"E18.5.1.2")])],"isStart":false});
            var Q113;
            Q113=makeQuery(id+"F3.opExtrude","CAP_EDGE",EDGE,{"disambiguationData":[OSD([sQuery(id+"F0.wireOp",EDGE,"E18.5.1.1")])],"isStart":false});
            var Q114;
            Q114=makeQuery(id+"F3.opExtrude","CAP_EDGE",EDGE,{"disambiguationData":[OSD([sQuery(id+"F0.wireOp",EDGE,"E18.5.0.1")])],"isStart":false});
            var Q115;
            Q115=makeQuery(id+"F3.opExtrude","CAP_EDGE",EDGE,{"disambiguationData":[OSD([sQuery(id+"F0.wireOp",EDGE,"E18.5.0.2")])],"isStart":false});
            var Q116;
            Q116=makeQuery(id+"F3.opExtrude","CAP_EDGE",EDGE,{"disambiguationData":[OSD([sQuery(id+"F0.wireOp",EDGE,"E18.4.0.4")])],"isStart":false});
            var Q117;
            Q117=makeQuery(id+"F3.opExtrude","CAP_EDGE",EDGE,{"disambiguationData":[OSD([sQuery(id+"F0.wireOp",EDGE,"E18.4.0.3")])],"isStart":false});
            var Q118;
            Q118=makeQuery(id+"F3.opExtrude","CAP_EDGE",EDGE,{"disambiguationData":[OSD([sQuery(id+"F0.wireOp",EDGE,"E18.4.0.1")])],"isStart":false});
            var Q119;
            Q119=makeQuery(id+"F3.opExtrude","CAP_EDGE",EDGE,{"disambiguationData":[OSD([sQuery(id+"F0.wireOp",EDGE,"E18.4.0.2")])],"isStart":false});
            fillet(context, id + "F4", {"entities" : qUnion([Q0, Q1, Q2, Q3, Q4, Q5, Q6, Q7, Q8, Q9, Q10, Q11, Q12, Q13, Q14, Q15, Q16, Q17, Q18, Q19, Q20, Q21, Q22, Q23, Q24, Q25, Q26, Q27, Q28, Q29, Q30, Q31, Q32, Q33, Q34, Q35, Q36, Q37, Q38, Q39, Q40, Q41, Q42, Q43, Q44, Q45, Q46, Q47, Q48, Q49, Q50, Q51, Q52, Q53, Q54, Q55, Q56, Q57, Q58, Q59, Q60, Q61, Q62, Q63, Q64, Q65, Q66, Q67, Q68, Q69, Q70, Q71, Q72, Q73, Q74, Q75, Q76, Q77, Q78, Q79, Q80, Q81, Q82, Q83, Q84, Q85, Q86, Q87, Q88, Q89, Q90, Q91, Q92, Q93, Q94, Q95, Q96, Q97, Q98, Q99, Q100, Q101, Q102, Q103, Q104, Q105, Q106, Q107, Q108, Q109, Q110, Q111, Q112, Q113, Q114, Q115, Q116, Q117, Q118, Q119]), "radius" : 0.5 * mm, "tangentPropagation" : true, "allowEdgeOverflow" : false});
        }
        {
            var Q0;
            {var subQ0=sQuery(id+"F0.wireOp",EDGE,"E25");Q0=makeQuery(id+"F2.opExtrude","CAP_EDGE",EDGE,{"disambiguationData":[OSD([subQ0]),TDD([makeQuery(id+"F0.imprint","IMPRINT",EDGE,{"disambiguationData":[TD([[makeQuery(id+"F0.imprint","INTERSECT",VERTEX,{"disambiguationData":[OD(0.0)],"derivedFrom":[sQuery(id+"F0.wireOp",EDGE,"E20.top"),subQ0]}),-1.0]])],"derivedFrom":subQ0})])],"isStart":false});}
            var Q1;
            {var subQ0=sQuery(id+"F0.wireOp",EDGE,"E24");Q1=makeQuery(id+"F2.opExtrude","CAP_EDGE",EDGE,{"disambiguationData":[OSD([subQ0]),TDD([makeQuery(id+"F0.imprint","IMPRINT",EDGE,{"disambiguationData":[TD([[makeQuery(id+"F0.imprint","INTERSECT",VERTEX,{"disambiguationData":[OD(0.0)],"derivedFrom":[sQuery(id+"F0.wireOp",EDGE,"E20.top"),subQ0]}),-1.0]])],"derivedFrom":subQ0})])],"isStart":false});}
            var Q2;
            {var subQ0=sQuery(id+"F0.wireOp",EDGE,"E32.MirrorCS");Q2=makeQuery(id+"F2.opExtrude","CAP_EDGE",EDGE,{"disambiguationData":[OSD([subQ0]),TDD([makeQuery(id+"F0.imprint","IMPRINT",EDGE,{"disambiguationData":[TD([[makeQuery(id+"F0.imprint","INTERSECT",VERTEX,{"derivedFrom":[sQuery(id+"F0.wireOp",EDGE,"E24"),subQ0]}),-1.0]])],"derivedFrom":subQ0})])],"isStart":false});}
            var Q3;
            {var subQ0=sQuery(id+"F0.wireOp",EDGE,"E31.0");Q3=makeQuery(id+"F2.opExtrude","CAP_EDGE",EDGE,{"disambiguationData":[OSD([subQ0]),TDD([makeQuery(id+"F0.imprint","IMPRINT",EDGE,{"disambiguationData":[TD([[makeQuery(id+"F0.imprint","INTERSECT",VERTEX,{"derivedFrom":[sQuery(id+"F0.wireOp",EDGE,"E26"),subQ0]}),-1.0]])],"derivedFrom":subQ0})])],"isStart":false});}
            var Q4;
            {var subQ0=sQuery(id+"F0.wireOp",EDGE,"E32.MirrorCS");Q4=makeQuery(id+"F2.opExtrude","CAP_EDGE",EDGE,{"disambiguationData":[OSD([subQ0]),TDD([makeQuery(id+"F0.imprint","IMPRINT",EDGE,{"disambiguationData":[TD([[makeQuery(id+"F0.imprint","INTERSECT",VERTEX,{"derivedFrom":[sQuery(id+"F0.wireOp",EDGE,"E26"),subQ0]}),-1.0]])],"derivedFrom":subQ0})])],"isStart":false});}
            var Q5;
            {var subQ0=sQuery(id+"F0.wireOp",EDGE,"E26");Q5=makeQuery(id+"F2.opExtrude","CAP_EDGE",EDGE,{"disambiguationData":[OSD([subQ0]),TDD([makeQuery(id+"F0.imprint","IMPRINT",EDGE,{"disambiguationData":[TD([[makeQuery(id+"F0.imprint","INTERSECT",VERTEX,{"disambiguationData":[OD(0.0)],"derivedFrom":[sQuery(id+"F0.wireOp",EDGE,"E20.top"),subQ0]}),-1.0]])],"derivedFrom":subQ0})])],"isStart":false});}
            var Q6;
            {var subQ0=sQuery(id+"F0.wireOp",EDGE,"E27");Q6=makeQuery(id+"F2.opExtrude","CAP_EDGE",EDGE,{"disambiguationData":[OSD([subQ0]),TDD([makeQuery(id+"F0.imprint","IMPRINT",EDGE,{"disambiguationData":[TD([[makeQuery(id+"F0.imprint","INTERSECT",VERTEX,{"derivedFrom":[subQ0,sQuery(id+"F0.wireOp",EDGE,"E31.0")]}),-1.0]])],"derivedFrom":subQ0})])],"isStart":false});}
            var Q7;
            {var subQ0=sQuery(id+"F0.wireOp",EDGE,"E32.MirrorCS");Q7=makeQuery(id+"F2.opExtrude","CAP_EDGE",EDGE,{"disambiguationData":[OSD([subQ0]),TDD([makeQuery(id+"F0.imprint","IMPRINT",EDGE,{"disambiguationData":[TD([[makeQuery(id+"F0.imprint","INTERSECT",VERTEX,{"derivedFrom":[sQuery(id+"F0.wireOp",EDGE,"E20.top"),subQ0]}),-1.0]])],"derivedFrom":subQ0})])],"isStart":false});}
            var Q8;
            {var subQ0=sQuery(id+"F0.wireOp",EDGE,"E31.0");Q8=makeQuery(id+"F2.opExtrude","CAP_EDGE",EDGE,{"disambiguationData":[OSD([subQ0]),TDD([makeQuery(id+"F0.imprint","IMPRINT",EDGE,{"disambiguationData":[TD([[makeQuery(id+"F0.imprint","INTERSECT",VERTEX,{"derivedFrom":[subQ0,sQuery(id+"F0.wireOp",EDGE,"E34.MirrorCS")]}),-1.0]])],"derivedFrom":subQ0})])],"isStart":false});}
            var Q9;
            {var subQ0=sQuery(id+"F0.wireOp",EDGE,"E26");Q9=makeQuery(id+"F2.opExtrude","CAP_EDGE",EDGE,{"disambiguationData":[OSD([subQ0]),TDD([makeQuery(id+"F0.imprint","IMPRINT",EDGE,{"disambiguationData":[TD([[makeQuery(id+"F0.imprint","INTERSECT",VERTEX,{"derivedFrom":[subQ0,sQuery(id+"F0.wireOp",EDGE,"E31.0")]}),-1.0]])],"derivedFrom":subQ0})])],"isStart":false});}
            var Q10;
            {var subQ0=sQuery(id+"F0.wireOp",EDGE,"E34.MirrorCS");Q10=makeQuery(id+"F2.opExtrude","CAP_EDGE",EDGE,{"disambiguationData":[OSD([subQ0]),TDD([makeQuery(id+"F0.imprint","IMPRINT",EDGE,{"disambiguationData":[TD([[makeQuery(id+"F0.imprint","INTERSECT",VERTEX,{"derivedFrom":[sQuery(id+"F0.wireOp",EDGE,"E31.0"),subQ0]}),-1.0]])],"derivedFrom":subQ0})])],"isStart":false});}
            var Q11;
            {var subQ0=sQuery(id+"F0.wireOp",EDGE,"E33.0");Q11=makeQuery(id+"F2.opExtrude","CAP_EDGE",EDGE,{"disambiguationData":[OSD([subQ0]),TDD([makeQuery(id+"F0.imprint","IMPRINT",EDGE,{"disambiguationData":[TD([[makeQuery(id+"F0.imprint","INTERSECT",VERTEX,{"derivedFrom":[subQ0,sQuery(id+"F0.wireOp",EDGE,"E36.MirrorCS")]}),-1.0]])],"derivedFrom":subQ0})])],"isStart":false});}
            var Q12;
            {var subQ0=sQuery(id+"F0.wireOp",EDGE,"E36.MirrorCS");Q12=makeQuery(id+"F2.opExtrude","CAP_EDGE",EDGE,{"disambiguationData":[OSD([subQ0]),TDD([makeQuery(id+"F0.imprint","IMPRINT",EDGE,{"disambiguationData":[TD([[makeQuery(id+"F0.imprint","INTERSECT",VERTEX,{"derivedFrom":[sQuery(id+"F0.wireOp",EDGE,"E33.0"),subQ0]}),-1.0]])],"derivedFrom":subQ0})])],"isStart":false});}
            var Q13;
            {var subQ0=sQuery(id+"F0.wireOp",EDGE,"E35.0");Q13=makeQuery(id+"F2.opExtrude","CAP_EDGE",EDGE,{"disambiguationData":[OSD([subQ0]),TDD([makeQuery(id+"F0.imprint","IMPRINT",EDGE,{"disambiguationData":[TD([[makeQuery(id+"F0.imprint","INTERSECT",VERTEX,{"derivedFrom":[subQ0,sQuery(id+"F0.wireOp",EDGE,"E38.0")]}),-1.0]])],"derivedFrom":subQ0})])],"isStart":false});}
            var Q14;
            {var subQ0=sQuery(id+"F0.wireOp",EDGE,"E38.0");Q14=makeQuery(id+"F2.opExtrude","CAP_EDGE",EDGE,{"disambiguationData":[OSD([subQ0]),TDD([makeQuery(id+"F0.imprint","IMPRINT",EDGE,{"disambiguationData":[TD([[makeQuery(id+"F0.imprint","INTERSECT",VERTEX,{"derivedFrom":[sQuery(id+"F0.wireOp",EDGE,"E35.0"),subQ0]}),-1.0]])],"derivedFrom":subQ0})])],"isStart":false});}
            var Q15;
            {var subQ0=sQuery(id+"F0.wireOp",EDGE,"E37.0");Q15=makeQuery(id+"F2.opExtrude","CAP_EDGE",EDGE,{"disambiguationData":[OSD([subQ0]),TDD([makeQuery(id+"F0.imprint","IMPRINT",EDGE,{"disambiguationData":[TD([[makeQuery(id+"F0.imprint","INTERSECT",VERTEX,{"derivedFrom":[subQ0,sQuery(id+"F0.wireOp",EDGE,"E40.0")]}),-1.0]])],"derivedFrom":subQ0})])],"isStart":false});}
            var Q16;
            {var subQ0=sQuery(id+"F0.wireOp",EDGE,"E40.0");Q16=makeQuery(id+"F2.opExtrude","CAP_EDGE",EDGE,{"disambiguationData":[OSD([subQ0]),TDD([makeQuery(id+"F0.imprint","IMPRINT",EDGE,{"disambiguationData":[TD([[makeQuery(id+"F0.imprint","INTERSECT",VERTEX,{"derivedFrom":[sQuery(id+"F0.wireOp",EDGE,"E37.0"),subQ0]}),-1.0]])],"derivedFrom":subQ0})])],"isStart":false});}
            var Q17;
            {var subQ0=sQuery(id+"F0.wireOp",EDGE,"E39.0");Q17=makeQuery(id+"F2.opExtrude","CAP_EDGE",EDGE,{"disambiguationData":[OSD([subQ0]),TDD([makeQuery(id+"F0.imprint","IMPRINT",EDGE,{"disambiguationData":[TD([[makeQuery(id+"F0.imprint","INTERSECT",VERTEX,{"derivedFrom":[subQ0,sQuery(id+"F0.wireOp",EDGE,"E44.0")]}),-1.0]])],"derivedFrom":subQ0})])],"isStart":false});}
            var Q18;
            {var subQ0=sQuery(id+"F0.wireOp",EDGE,"E44.0");Q18=makeQuery(id+"F2.opExtrude","CAP_EDGE",EDGE,{"disambiguationData":[OSD([subQ0]),TDD([makeQuery(id+"F0.imprint","IMPRINT",EDGE,{"disambiguationData":[TD([[makeQuery(id+"F0.imprint","INTERSECT",VERTEX,{"derivedFrom":[sQuery(id+"F0.wireOp",EDGE,"E39.0"),subQ0]}),-1.0]])],"derivedFrom":subQ0})])],"isStart":false});}
            var Q19;
            {var subQ0=sQuery(id+"F0.wireOp",EDGE,"E43.0");Q19=makeQuery(id+"F2.opExtrude","CAP_EDGE",EDGE,{"disambiguationData":[OSD([subQ0]),TDD([makeQuery(id+"F0.imprint","IMPRINT",EDGE,{"disambiguationData":[TD([[makeQuery(id+"F0.imprint","INTERSECT",VERTEX,{"derivedFrom":[sQuery(id+"F0.wireOp",EDGE,"E42.0"),subQ0]}),-1.0]])],"derivedFrom":subQ0})])],"isStart":false});}
            var Q20;
            {var subQ0=sQuery(id+"F0.wireOp",EDGE,"E42.0");Q20=makeQuery(id+"F2.opExtrude","CAP_EDGE",EDGE,{"disambiguationData":[OSD([subQ0]),TDD([makeQuery(id+"F0.imprint","IMPRINT",EDGE,{"disambiguationData":[TD([[makeQuery(id+"F0.imprint","INTERSECT",VERTEX,{"derivedFrom":[subQ0,sQuery(id+"F0.wireOp",EDGE,"E43.0")]}),-1.0]])],"derivedFrom":subQ0})])],"isStart":false});}
            var Q21;
            {var subQ0=sQuery(id+"F0.wireOp",EDGE,"E41.0");Q21=makeQuery(id+"F2.opExtrude","CAP_EDGE",EDGE,{"disambiguationData":[OSD([subQ0]),TDD([makeQuery(id+"F0.imprint","IMPRINT",EDGE,{"disambiguationData":[TD([[makeQuery(id+"F0.imprint","INTERSECT",VERTEX,{"derivedFrom":[sQuery(id+"F0.wireOp",EDGE,"E20.top"),subQ0]}),-1.0]])],"derivedFrom":subQ0})])],"isStart":false});}
            var Q22;
            {var subQ0=sQuery(id+"F0.wireOp",EDGE,"E27");Q22=makeQuery(id+"F2.opExtrude","CAP_EDGE",EDGE,{"disambiguationData":[OSD([subQ0]),TDD([makeQuery(id+"F0.imprint","IMPRINT",EDGE,{"disambiguationData":[TD([[makeQuery(id+"F0.imprint","INTERSECT",VERTEX,{"disambiguationData":[OD(1.0)],"derivedFrom":[sQuery(id+"F0.wireOp",EDGE,"E20.top"),subQ0]}),1.0]])],"derivedFrom":subQ0})])],"isStart":false});}
            var Q23;
            {var subQ0=sQuery(id+"F0.wireOp",EDGE,"E26");Q23=makeQuery(id+"F2.opExtrude","CAP_EDGE",EDGE,{"disambiguationData":[OSD([subQ0]),TDD([makeQuery(id+"F0.imprint","IMPRINT",EDGE,{"disambiguationData":[TD([[makeQuery(id+"F0.imprint","INTERSECT",VERTEX,{"derivedFrom":[subQ0,sQuery(id+"F0.wireOp",EDGE,"E42.0")]}),1.0]])],"derivedFrom":subQ0})])],"isStart":false});}
            var Q24;
            {var subQ0=sQuery(id+"F0.wireOp",EDGE,"E27");Q24=makeQuery(id+"F2.opExtrude","CAP_EDGE",EDGE,{"disambiguationData":[OSD([subQ0]),TDD([makeQuery(id+"F0.imprint","IMPRINT",EDGE,{"disambiguationData":[TD([[makeQuery(id+"F0.imprint","INTERSECT",VERTEX,{"derivedFrom":[subQ0,sQuery(id+"F0.wireOp",EDGE,"E43.0")]}),-1.0]])],"derivedFrom":subQ0})])],"isStart":false});}
            var Q25;
            {var subQ0=sQuery(id+"F0.wireOp",EDGE,"E27");Q25=makeQuery(id+"F2.opExtrude","CAP_EDGE",EDGE,{"disambiguationData":[OSD([subQ0]),TDD([makeQuery(id+"F0.imprint","IMPRINT",EDGE,{"disambiguationData":[TD([[makeQuery(id+"F0.imprint","INTERSECT",VERTEX,{"derivedFrom":[subQ0,sQuery(id+"F0.wireOp",EDGE,"E39.0")]}),-1.0]])],"derivedFrom":subQ0})])],"isStart":false});}
            var Q26;
            {var subQ0=sQuery(id+"F0.wireOp",EDGE,"E26");Q26=makeQuery(id+"F2.opExtrude","CAP_EDGE",EDGE,{"disambiguationData":[OSD([subQ0]),TDD([makeQuery(id+"F0.imprint","IMPRINT",EDGE,{"disambiguationData":[TD([[makeQuery(id+"F0.imprint","INTERSECT",VERTEX,{"derivedFrom":[subQ0,sQuery(id+"F0.wireOp",EDGE,"E39.0")]}),-1.0]])],"derivedFrom":subQ0})])],"isStart":false});}
            var Q27;
            {var subQ0=sQuery(id+"F0.wireOp",EDGE,"E26");Q27=makeQuery(id+"F2.opExtrude","CAP_EDGE",EDGE,{"disambiguationData":[OSD([subQ0]),TDD([makeQuery(id+"F0.imprint","IMPRINT",EDGE,{"disambiguationData":[TD([[makeQuery(id+"F0.imprint","INTERSECT",VERTEX,{"derivedFrom":[subQ0,sQuery(id+"F0.wireOp",EDGE,"E37.0")]}),-1.0]])],"derivedFrom":subQ0})])],"isStart":false});}
            var Q28;
            {var subQ0=sQuery(id+"F0.wireOp",EDGE,"E27");Q28=makeQuery(id+"F2.opExtrude","CAP_EDGE",EDGE,{"disambiguationData":[OSD([subQ0]),TDD([makeQuery(id+"F0.imprint","IMPRINT",EDGE,{"disambiguationData":[TD([[makeQuery(id+"F0.imprint","INTERSECT",VERTEX,{"derivedFrom":[subQ0,sQuery(id+"F0.wireOp",EDGE,"E37.0")]}),-1.0]])],"derivedFrom":subQ0})])],"isStart":false});}
            var Q29;
            {var subQ0=sQuery(id+"F0.wireOp",EDGE,"E26");Q29=makeQuery(id+"F2.opExtrude","CAP_EDGE",EDGE,{"disambiguationData":[OSD([subQ0]),TDD([makeQuery(id+"F0.imprint","IMPRINT",EDGE,{"disambiguationData":[TD([[makeQuery(id+"F0.imprint","INTERSECT",VERTEX,{"derivedFrom":[subQ0,sQuery(id+"F0.wireOp",EDGE,"E35.0")]}),-1.0]])],"derivedFrom":subQ0})])],"isStart":false});}
            var Q30;
            {var subQ0=sQuery(id+"F0.wireOp",EDGE,"E27");Q30=makeQuery(id+"F2.opExtrude","CAP_EDGE",EDGE,{"disambiguationData":[OSD([subQ0]),TDD([makeQuery(id+"F0.imprint","IMPRINT",EDGE,{"disambiguationData":[TD([[makeQuery(id+"F0.imprint","INTERSECT",VERTEX,{"derivedFrom":[subQ0,sQuery(id+"F0.wireOp",EDGE,"E35.0")]}),-1.0]])],"derivedFrom":subQ0})])],"isStart":false});}
            var Q31;
            {var subQ0=sQuery(id+"F0.wireOp",EDGE,"E27");Q31=makeQuery(id+"F2.opExtrude","CAP_EDGE",EDGE,{"disambiguationData":[OSD([subQ0]),TDD([makeQuery(id+"F0.imprint","IMPRINT",EDGE,{"disambiguationData":[TD([[makeQuery(id+"F0.imprint","INTERSECT",VERTEX,{"derivedFrom":[subQ0,sQuery(id+"F0.wireOp",EDGE,"E33.0")]}),-1.0]])],"derivedFrom":subQ0})])],"isStart":false});}
            var Q32;
            {var subQ0=sQuery(id+"F0.wireOp",EDGE,"E26");Q32=makeQuery(id+"F2.opExtrude","CAP_EDGE",EDGE,{"disambiguationData":[OSD([subQ0]),TDD([makeQuery(id+"F0.imprint","IMPRINT",EDGE,{"disambiguationData":[TD([[makeQuery(id+"F0.imprint","INTERSECT",VERTEX,{"derivedFrom":[subQ0,sQuery(id+"F0.wireOp",EDGE,"E33.0")]}),-1.0]])],"derivedFrom":subQ0})])],"isStart":false});}
            var Q33;
            {var subQ0=sQuery(id+"F0.wireOp",EDGE,"E26");Q33=makeQuery(id+"F2.opExtrude","CAP_EDGE",EDGE,{"disambiguationData":[OSD([subQ0]),TDD([makeQuery(id+"F0.imprint","IMPRINT",EDGE,{"disambiguationData":[TD([[makeQuery(id+"F0.imprint","INTERSECT",VERTEX,{"disambiguationData":[OD(1.0)],"derivedFrom":[sQuery(id+"F0.wireOp",EDGE,"E20.top"),subQ0]}),1.0]])],"derivedFrom":subQ0})])],"isStart":false});}
            var Q34;
            {var subQ0=sQuery(id+"F0.wireOp",EDGE,"E41.0");Q34=makeQuery(id+"F2.opExtrude","CAP_EDGE",EDGE,{"disambiguationData":[OSD([subQ0]),TDD([makeQuery(id+"F0.imprint","IMPRINT",EDGE,{"disambiguationData":[TD([[makeQuery(id+"F0.imprint","INTERSECT",VERTEX,{"derivedFrom":[sQuery(id+"F0.wireOp",EDGE,"E26"),subQ0]}),-1.0]])],"derivedFrom":subQ0})])],"isStart":false});}
            var Q35;
            {var subQ0=sQuery(id+"F0.wireOp",EDGE,"E42.0");Q35=makeQuery(id+"F2.opExtrude","CAP_EDGE",EDGE,{"disambiguationData":[OSD([subQ0]),TDD([makeQuery(id+"F0.imprint","IMPRINT",EDGE,{"disambiguationData":[TD([[makeQuery(id+"F0.imprint","INTERSECT",VERTEX,{"derivedFrom":[sQuery(id+"F0.wireOp",EDGE,"E26"),subQ0]}),-1.0]])],"derivedFrom":subQ0})])],"isStart":false});}
            var Q36;
            {var subQ0=sQuery(id+"F0.wireOp",EDGE,"E43.0");Q36=makeQuery(id+"F2.opExtrude","CAP_EDGE",EDGE,{"disambiguationData":[OSD([subQ0]),TDD([makeQuery(id+"F0.imprint","IMPRINT",EDGE,{"disambiguationData":[TD([[makeQuery(id+"F0.imprint","INTERSECT",VERTEX,{"derivedFrom":[sQuery(id+"F0.wireOp",EDGE,"E26"),subQ0]}),-1.0]])],"derivedFrom":subQ0})])],"isStart":false});}
            var Q37;
            {var subQ0=sQuery(id+"F0.wireOp",EDGE,"E44.0");Q37=makeQuery(id+"F2.opExtrude","CAP_EDGE",EDGE,{"disambiguationData":[OSD([subQ0]),TDD([makeQuery(id+"F0.imprint","IMPRINT",EDGE,{"disambiguationData":[TD([[makeQuery(id+"F0.imprint","INTERSECT",VERTEX,{"derivedFrom":[sQuery(id+"F0.wireOp",EDGE,"E26"),subQ0]}),-1.0]])],"derivedFrom":subQ0})])],"isStart":false});}
            var Q38;
            {var subQ0=sQuery(id+"F0.wireOp",EDGE,"E39.0");Q38=makeQuery(id+"F2.opExtrude","CAP_EDGE",EDGE,{"disambiguationData":[OSD([subQ0]),TDD([makeQuery(id+"F0.imprint","IMPRINT",EDGE,{"disambiguationData":[TD([[makeQuery(id+"F0.imprint","INTERSECT",VERTEX,{"derivedFrom":[sQuery(id+"F0.wireOp",EDGE,"E26"),subQ0]}),-1.0]])],"derivedFrom":subQ0})])],"isStart":false});}
            var Q39;
            {var subQ0=sQuery(id+"F0.wireOp",EDGE,"E40.0");Q39=makeQuery(id+"F2.opExtrude","CAP_EDGE",EDGE,{"disambiguationData":[OSD([subQ0]),TDD([makeQuery(id+"F0.imprint","IMPRINT",EDGE,{"disambiguationData":[TD([[makeQuery(id+"F0.imprint","INTERSECT",VERTEX,{"derivedFrom":[sQuery(id+"F0.wireOp",EDGE,"E26"),subQ0]}),-1.0]])],"derivedFrom":subQ0})])],"isStart":false});}
            var Q40;
            {var subQ0=sQuery(id+"F0.wireOp",EDGE,"E38.0");Q40=makeQuery(id+"F2.opExtrude","CAP_EDGE",EDGE,{"disambiguationData":[OSD([subQ0]),TDD([makeQuery(id+"F0.imprint","IMPRINT",EDGE,{"disambiguationData":[TD([[makeQuery(id+"F0.imprint","INTERSECT",VERTEX,{"derivedFrom":[sQuery(id+"F0.wireOp",EDGE,"E26"),subQ0]}),-1.0]])],"derivedFrom":subQ0})])],"isStart":false});}
            var Q41;
            {var subQ0=sQuery(id+"F0.wireOp",EDGE,"E35.0");Q41=makeQuery(id+"F2.opExtrude","CAP_EDGE",EDGE,{"disambiguationData":[OSD([subQ0]),TDD([makeQuery(id+"F0.imprint","IMPRINT",EDGE,{"disambiguationData":[TD([[makeQuery(id+"F0.imprint","INTERSECT",VERTEX,{"derivedFrom":[sQuery(id+"F0.wireOp",EDGE,"E26"),subQ0]}),-1.0]])],"derivedFrom":subQ0})])],"isStart":false});}
            var Q42;
            {var subQ0=sQuery(id+"F0.wireOp",EDGE,"E36.MirrorCS");Q42=makeQuery(id+"F2.opExtrude","CAP_EDGE",EDGE,{"disambiguationData":[OSD([subQ0]),TDD([makeQuery(id+"F0.imprint","IMPRINT",EDGE,{"disambiguationData":[TD([[makeQuery(id+"F0.imprint","INTERSECT",VERTEX,{"derivedFrom":[sQuery(id+"F0.wireOp",EDGE,"E26"),subQ0]}),-1.0]])],"derivedFrom":subQ0})])],"isStart":false});}
            var Q43;
            {var subQ0=sQuery(id+"F0.wireOp",EDGE,"E33.0");Q43=makeQuery(id+"F2.opExtrude","CAP_EDGE",EDGE,{"disambiguationData":[OSD([subQ0]),TDD([makeQuery(id+"F0.imprint","IMPRINT",EDGE,{"disambiguationData":[TD([[makeQuery(id+"F0.imprint","INTERSECT",VERTEX,{"derivedFrom":[sQuery(id+"F0.wireOp",EDGE,"E26"),subQ0]}),-1.0]])],"derivedFrom":subQ0})])],"isStart":false});}
            var Q44;
            {var subQ0=sQuery(id+"F0.wireOp",EDGE,"E34.MirrorCS");Q44=makeQuery(id+"F2.opExtrude","CAP_EDGE",EDGE,{"disambiguationData":[OSD([subQ0]),TDD([makeQuery(id+"F0.imprint","IMPRINT",EDGE,{"disambiguationData":[TD([[makeQuery(id+"F0.imprint","INTERSECT",VERTEX,{"derivedFrom":[sQuery(id+"F0.wireOp",EDGE,"E26"),subQ0]}),-1.0]])],"derivedFrom":subQ0})])],"isStart":false});}
            var Q45;
            {var subQ0=sQuery(id+"F0.wireOp",EDGE,"E25");Q45=makeQuery(id+"F2.opExtrude","CAP_EDGE",EDGE,{"disambiguationData":[OSD([subQ0]),TDD([makeQuery(id+"F0.imprint","IMPRINT",EDGE,{"disambiguationData":[TD([[makeQuery(id+"F0.imprint","INTERSECT",VERTEX,{"derivedFrom":[subQ0,sQuery(id+"F0.wireOp",EDGE,"E31.0")]}),-1.0]])],"derivedFrom":subQ0})])],"isStart":false});}
            var Q46;
            {var subQ0=sQuery(id+"F0.wireOp",EDGE,"E24");Q46=makeQuery(id+"F2.opExtrude","CAP_EDGE",EDGE,{"disambiguationData":[OSD([subQ0]),TDD([makeQuery(id+"F0.imprint","IMPRINT",EDGE,{"disambiguationData":[TD([[makeQuery(id+"F0.imprint","INTERSECT",VERTEX,{"derivedFrom":[subQ0,sQuery(id+"F0.wireOp",EDGE,"E31.0")]}),-1.0]])],"derivedFrom":subQ0})])],"isStart":false});}
            var Q47;
            {var subQ0=sQuery(id+"F0.wireOp",EDGE,"E25");Q47=makeQuery(id+"F2.opExtrude","CAP_EDGE",EDGE,{"disambiguationData":[OSD([subQ0]),TDD([makeQuery(id+"F0.imprint","IMPRINT",EDGE,{"disambiguationData":[TD([[makeQuery(id+"F0.imprint","INTERSECT",VERTEX,{"derivedFrom":[subQ0,sQuery(id+"F0.wireOp",EDGE,"E33.0")]}),-1.0]])],"derivedFrom":subQ0})])],"isStart":false});}
            var Q48;
            {var subQ0=sQuery(id+"F0.wireOp",EDGE,"E24");Q48=makeQuery(id+"F2.opExtrude","CAP_EDGE",EDGE,{"disambiguationData":[OSD([subQ0]),TDD([makeQuery(id+"F0.imprint","IMPRINT",EDGE,{"disambiguationData":[TD([[makeQuery(id+"F0.imprint","INTERSECT",VERTEX,{"derivedFrom":[subQ0,sQuery(id+"F0.wireOp",EDGE,"E33.0")]}),-1.0]])],"derivedFrom":subQ0})])],"isStart":false});}
            var Q49;
            {var subQ0=sQuery(id+"F0.wireOp",EDGE,"E25");Q49=makeQuery(id+"F2.opExtrude","CAP_EDGE",EDGE,{"disambiguationData":[OSD([subQ0]),TDD([makeQuery(id+"F0.imprint","IMPRINT",EDGE,{"disambiguationData":[TD([[makeQuery(id+"F0.imprint","INTERSECT",VERTEX,{"derivedFrom":[subQ0,sQuery(id+"F0.wireOp",EDGE,"E35.0")]}),-1.0]])],"derivedFrom":subQ0})])],"isStart":false});}
            var Q50;
            {var subQ0=sQuery(id+"F0.wireOp",EDGE,"E24");Q50=makeQuery(id+"F2.opExtrude","CAP_EDGE",EDGE,{"disambiguationData":[OSD([subQ0]),TDD([makeQuery(id+"F0.imprint","IMPRINT",EDGE,{"disambiguationData":[TD([[makeQuery(id+"F0.imprint","INTERSECT",VERTEX,{"derivedFrom":[subQ0,sQuery(id+"F0.wireOp",EDGE,"E35.0")]}),-1.0]])],"derivedFrom":subQ0})])],"isStart":false});}
            var Q51;
            {var subQ0=sQuery(id+"F0.wireOp",EDGE,"E25");Q51=makeQuery(id+"F2.opExtrude","CAP_EDGE",EDGE,{"disambiguationData":[OSD([subQ0]),TDD([makeQuery(id+"F0.imprint","IMPRINT",EDGE,{"disambiguationData":[TD([[makeQuery(id+"F0.imprint","INTERSECT",VERTEX,{"derivedFrom":[subQ0,sQuery(id+"F0.wireOp",EDGE,"E37.0")]}),-1.0]])],"derivedFrom":subQ0})])],"isStart":false});}
            var Q52;
            {var subQ0=sQuery(id+"F0.wireOp",EDGE,"E24");Q52=makeQuery(id+"F2.opExtrude","CAP_EDGE",EDGE,{"disambiguationData":[OSD([subQ0]),TDD([makeQuery(id+"F0.imprint","IMPRINT",EDGE,{"disambiguationData":[TD([[makeQuery(id+"F0.imprint","INTERSECT",VERTEX,{"derivedFrom":[subQ0,sQuery(id+"F0.wireOp",EDGE,"E37.0")]}),-1.0]])],"derivedFrom":subQ0})])],"isStart":false});}
            var Q53;
            {var subQ0=sQuery(id+"F0.wireOp",EDGE,"E25");Q53=makeQuery(id+"F2.opExtrude","CAP_EDGE",EDGE,{"disambiguationData":[OSD([subQ0]),TDD([makeQuery(id+"F0.imprint","IMPRINT",EDGE,{"disambiguationData":[TD([[makeQuery(id+"F0.imprint","INTERSECT",VERTEX,{"derivedFrom":[subQ0,sQuery(id+"F0.wireOp",EDGE,"E39.0")]}),-1.0]])],"derivedFrom":subQ0})])],"isStart":false});}
            var Q54;
            {var subQ0=sQuery(id+"F0.wireOp",EDGE,"E24");Q54=makeQuery(id+"F2.opExtrude","CAP_EDGE",EDGE,{"disambiguationData":[OSD([subQ0]),TDD([makeQuery(id+"F0.imprint","IMPRINT",EDGE,{"disambiguationData":[TD([[makeQuery(id+"F0.imprint","INTERSECT",VERTEX,{"derivedFrom":[subQ0,sQuery(id+"F0.wireOp",EDGE,"E39.0")]}),-1.0]])],"derivedFrom":subQ0})])],"isStart":false});}
            var Q55;
            {var subQ0=sQuery(id+"F0.wireOp",EDGE,"E25");Q55=makeQuery(id+"F2.opExtrude","CAP_EDGE",EDGE,{"disambiguationData":[OSD([subQ0]),TDD([makeQuery(id+"F0.imprint","IMPRINT",EDGE,{"disambiguationData":[TD([[makeQuery(id+"F0.imprint","INTERSECT",VERTEX,{"derivedFrom":[subQ0,sQuery(id+"F0.wireOp",EDGE,"E43.0")]}),-1.0]])],"derivedFrom":subQ0})])],"isStart":false});}
            var Q56;
            {var subQ0=sQuery(id+"F0.wireOp",EDGE,"E24");Q56=makeQuery(id+"F2.opExtrude","CAP_EDGE",EDGE,{"disambiguationData":[OSD([subQ0]),TDD([makeQuery(id+"F0.imprint","IMPRINT",EDGE,{"disambiguationData":[TD([[makeQuery(id+"F0.imprint","INTERSECT",VERTEX,{"derivedFrom":[subQ0,sQuery(id+"F0.wireOp",EDGE,"E42.0")]}),1.0]])],"derivedFrom":subQ0})])],"isStart":false});}
            var Q57;
            {var subQ0=sQuery(id+"F0.wireOp",EDGE,"E24");Q57=makeQuery(id+"F2.opExtrude","CAP_EDGE",EDGE,{"disambiguationData":[OSD([subQ0]),TDD([makeQuery(id+"F0.imprint","IMPRINT",EDGE,{"disambiguationData":[TD([[makeQuery(id+"F0.imprint","INTERSECT",VERTEX,{"disambiguationData":[OD(1.0)],"derivedFrom":[sQuery(id+"F0.wireOp",EDGE,"E20.top"),subQ0]}),1.0]])],"derivedFrom":subQ0})])],"isStart":false});}
            var Q58;
            {var subQ0=sQuery(id+"F0.wireOp",EDGE,"E41.0");Q58=makeQuery(id+"F2.opExtrude","CAP_EDGE",EDGE,{"disambiguationData":[OSD([subQ0]),TDD([makeQuery(id+"F0.imprint","IMPRINT",EDGE,{"disambiguationData":[TD([[makeQuery(id+"F0.imprint","INTERSECT",VERTEX,{"derivedFrom":[sQuery(id+"F0.wireOp",EDGE,"E24"),subQ0]}),-1.0]])],"derivedFrom":subQ0})])],"isStart":false});}
            var Q59;
            {var subQ0=sQuery(id+"F0.wireOp",EDGE,"E42.0");Q59=makeQuery(id+"F2.opExtrude","CAP_EDGE",EDGE,{"disambiguationData":[OSD([subQ0]),TDD([makeQuery(id+"F0.imprint","IMPRINT",EDGE,{"disambiguationData":[TD([[makeQuery(id+"F0.imprint","INTERSECT",VERTEX,{"derivedFrom":[sQuery(id+"F0.wireOp",EDGE,"E24"),subQ0]}),-1.0]])],"derivedFrom":subQ0})])],"isStart":false});}
            var Q60;
            {var subQ0=sQuery(id+"F0.wireOp",EDGE,"E25");Q60=makeQuery(id+"F2.opExtrude","CAP_EDGE",EDGE,{"disambiguationData":[OSD([subQ0]),TDD([makeQuery(id+"F0.imprint","IMPRINT",EDGE,{"disambiguationData":[TD([[makeQuery(id+"F0.imprint","INTERSECT",VERTEX,{"disambiguationData":[OD(1.0)],"derivedFrom":[sQuery(id+"F0.wireOp",EDGE,"E20.top"),subQ0]}),1.0]])],"derivedFrom":subQ0})])],"isStart":false});}
            var Q61;
            {var subQ0=sQuery(id+"F0.wireOp",EDGE,"E43.0");Q61=makeQuery(id+"F2.opExtrude","CAP_EDGE",EDGE,{"disambiguationData":[OSD([subQ0]),TDD([makeQuery(id+"F0.imprint","IMPRINT",EDGE,{"disambiguationData":[TD([[makeQuery(id+"F0.imprint","INTERSECT",VERTEX,{"derivedFrom":[sQuery(id+"F0.wireOp",EDGE,"E24"),subQ0]}),-1.0]])],"derivedFrom":subQ0})])],"isStart":false});}
            var Q62;
            {var subQ0=sQuery(id+"F0.wireOp",EDGE,"E44.0");Q62=makeQuery(id+"F2.opExtrude","CAP_EDGE",EDGE,{"disambiguationData":[OSD([subQ0]),TDD([makeQuery(id+"F0.imprint","IMPRINT",EDGE,{"disambiguationData":[TD([[makeQuery(id+"F0.imprint","INTERSECT",VERTEX,{"derivedFrom":[sQuery(id+"F0.wireOp",EDGE,"E24"),subQ0]}),-1.0]])],"derivedFrom":subQ0})])],"isStart":false});}
            var Q63;
            {var subQ0=sQuery(id+"F0.wireOp",EDGE,"E39.0");Q63=makeQuery(id+"F2.opExtrude","CAP_EDGE",EDGE,{"disambiguationData":[OSD([subQ0]),TDD([makeQuery(id+"F0.imprint","IMPRINT",EDGE,{"disambiguationData":[TD([[makeQuery(id+"F0.imprint","INTERSECT",VERTEX,{"derivedFrom":[sQuery(id+"F0.wireOp",EDGE,"E24"),subQ0]}),-1.0]])],"derivedFrom":subQ0})])],"isStart":false});}
            var Q64;
            {var subQ0=sQuery(id+"F0.wireOp",EDGE,"E40.0");Q64=makeQuery(id+"F2.opExtrude","CAP_EDGE",EDGE,{"disambiguationData":[OSD([subQ0]),TDD([makeQuery(id+"F0.imprint","IMPRINT",EDGE,{"disambiguationData":[TD([[makeQuery(id+"F0.imprint","INTERSECT",VERTEX,{"derivedFrom":[sQuery(id+"F0.wireOp",EDGE,"E24"),subQ0]}),-1.0]])],"derivedFrom":subQ0})])],"isStart":false});}
            var Q65;
            {var subQ0=sQuery(id+"F0.wireOp",EDGE,"E37.0");Q65=makeQuery(id+"F2.opExtrude","CAP_EDGE",EDGE,{"disambiguationData":[OSD([subQ0]),TDD([makeQuery(id+"F0.imprint","IMPRINT",EDGE,{"disambiguationData":[TD([[makeQuery(id+"F0.imprint","INTERSECT",VERTEX,{"derivedFrom":[sQuery(id+"F0.wireOp",EDGE,"E26"),subQ0]}),-1.0]])],"derivedFrom":subQ0})])],"isStart":false});}
            var Q66;
            {var subQ0=sQuery(id+"F0.wireOp",EDGE,"E37.0");Q66=makeQuery(id+"F2.opExtrude","CAP_EDGE",EDGE,{"disambiguationData":[OSD([subQ0]),TDD([makeQuery(id+"F0.imprint","IMPRINT",EDGE,{"disambiguationData":[TD([[makeQuery(id+"F0.imprint","INTERSECT",VERTEX,{"derivedFrom":[sQuery(id+"F0.wireOp",EDGE,"E24"),subQ0]}),-1.0]])],"derivedFrom":subQ0})])],"isStart":false});}
            var Q67;
            {var subQ0=sQuery(id+"F0.wireOp",EDGE,"E38.0");Q67=makeQuery(id+"F2.opExtrude","CAP_EDGE",EDGE,{"disambiguationData":[OSD([subQ0]),TDD([makeQuery(id+"F0.imprint","IMPRINT",EDGE,{"disambiguationData":[TD([[makeQuery(id+"F0.imprint","INTERSECT",VERTEX,{"derivedFrom":[sQuery(id+"F0.wireOp",EDGE,"E24"),subQ0]}),-1.0]])],"derivedFrom":subQ0})])],"isStart":false});}
            var Q68;
            {var subQ0=sQuery(id+"F0.wireOp",EDGE,"E35.0");Q68=makeQuery(id+"F2.opExtrude","CAP_EDGE",EDGE,{"disambiguationData":[OSD([subQ0]),TDD([makeQuery(id+"F0.imprint","IMPRINT",EDGE,{"disambiguationData":[TD([[makeQuery(id+"F0.imprint","INTERSECT",VERTEX,{"derivedFrom":[sQuery(id+"F0.wireOp",EDGE,"E24"),subQ0]}),-1.0]])],"derivedFrom":subQ0})])],"isStart":false});}
            var Q69;
            {var subQ0=sQuery(id+"F0.wireOp",EDGE,"E36.MirrorCS");Q69=makeQuery(id+"F2.opExtrude","CAP_EDGE",EDGE,{"disambiguationData":[OSD([subQ0]),TDD([makeQuery(id+"F0.imprint","IMPRINT",EDGE,{"disambiguationData":[TD([[makeQuery(id+"F0.imprint","INTERSECT",VERTEX,{"derivedFrom":[sQuery(id+"F0.wireOp",EDGE,"E24"),subQ0]}),-1.0]])],"derivedFrom":subQ0})])],"isStart":false});}
            var Q70;
            {var subQ0=sQuery(id+"F0.wireOp",EDGE,"E33.0");Q70=makeQuery(id+"F2.opExtrude","CAP_EDGE",EDGE,{"disambiguationData":[OSD([subQ0]),TDD([makeQuery(id+"F0.imprint","IMPRINT",EDGE,{"disambiguationData":[TD([[makeQuery(id+"F0.imprint","INTERSECT",VERTEX,{"derivedFrom":[sQuery(id+"F0.wireOp",EDGE,"E24"),subQ0]}),-1.0]])],"derivedFrom":subQ0})])],"isStart":false});}
            var Q71;
            {var subQ0=sQuery(id+"F0.wireOp",EDGE,"E34.MirrorCS");Q71=makeQuery(id+"F2.opExtrude","CAP_EDGE",EDGE,{"disambiguationData":[OSD([subQ0]),TDD([makeQuery(id+"F0.imprint","IMPRINT",EDGE,{"disambiguationData":[TD([[makeQuery(id+"F0.imprint","INTERSECT",VERTEX,{"derivedFrom":[sQuery(id+"F0.wireOp",EDGE,"E24"),subQ0]}),-1.0]])],"derivedFrom":subQ0})])],"isStart":false});}
            var Q72;
            {var subQ0=sQuery(id+"F0.wireOp",EDGE,"E31.0");Q72=makeQuery(id+"F2.opExtrude","CAP_EDGE",EDGE,{"disambiguationData":[OSD([subQ0]),TDD([makeQuery(id+"F0.imprint","IMPRINT",EDGE,{"disambiguationData":[TD([[makeQuery(id+"F0.imprint","INTERSECT",VERTEX,{"derivedFrom":[sQuery(id+"F0.wireOp",EDGE,"E24"),subQ0]}),-1.0]])],"derivedFrom":subQ0})])],"isStart":false});}
            var Q73;
            {var subQ0=sQuery(id+"F0.wireOp",EDGE,"E27");Q73=makeQuery(id+"F2.opExtrude","CAP_EDGE",EDGE,{"disambiguationData":[OSD([subQ0]),TDD([makeQuery(id+"F0.imprint","IMPRINT",EDGE,{"disambiguationData":[TD([[makeQuery(id+"F0.imprint","INTERSECT",VERTEX,{"disambiguationData":[OD(0.0)],"derivedFrom":[sQuery(id+"F0.wireOp",EDGE,"E20.top"),subQ0]}),-1.0]])],"derivedFrom":subQ0})])],"isStart":false});}
            fillet(context, id + "F5", {"entities" : qUnion([Q0, Q1, Q2, Q3, Q4, Q5, Q6, Q7, Q8, Q9, Q10, Q11, Q12, Q13, Q14, Q15, Q16, Q17, Q18, Q19, Q20, Q21, Q22, Q23, Q24, Q25, Q26, Q27, Q28, Q29, Q30, Q31, Q32, Q33, Q34, Q35, Q36, Q37, Q38, Q39, Q40, Q41, Q42, Q43, Q44, Q45, Q46, Q47, Q48, Q49, Q50, Q51, Q52, Q53, Q54, Q55, Q56, Q57, Q58, Q59, Q60, Q61, Q62, Q63, Q64, Q65, Q66, Q67, Q68, Q69, Q70, Q71, Q72, Q73]), "radius" : 0.5 * mm, "tangentPropagation" : true, "allowEdgeOverflow" : false});
        }
        {
            var Q0;
            Q0=makeQuery(id+"F1.opExtrude","SWEPT_FACE",FACE,{"disambiguationData":[OSD([sQuery(id+"F0.wireOp",EDGE,"E4")])]});
            var sketch = newSketch(context, id + "F6", { "sketchPlane" : qUnion([Q0])});
            skLineSegment(sketch, "E45.0", {"start": v(-19.33, 1.5) * mm, "end": v(-19.33, 0) * mm});
            skArc(sketch, "E45.1", {"start": v(-20.33, 1.5) * mm, "mid": v(-19.83, 2) * mm, "end": v(-19.33, 1.5) * mm});
            skLineSegment(sketch, "E45.2", {"start": v(-20.33, 1.5) * mm, "end": v(-20.33, 0) * mm});
            skLineSegment(sketch, "E46", {"start": v(-20.33, 0) * mm, "end": v(-19.33, 0) * mm});
            skLineSegment(sketch, "E47.0", {"start": v(-40.67, 1.5) * mm, "end": v(-40.67, 0) * mm});
            skArc(sketch, "E47.1", {"start": v(-40.67, 1.5) * mm, "mid": v(-40.17, 2) * mm, "end": v(-39.67, 1.5) * mm});
            skLineSegment(sketch, "E47.2", {"start": v(-39.67, 1.5) * mm, "end": v(-39.67, 0) * mm});
            skLineSegment(sketch, "E48", {"start": v(-40.67, 0) * mm, "end": v(-39.67, 0) * mm});
            skSolve(sketch);
        }
        {
            var Q0;
            Q0=qSketchRegion(id+"F6",true);
            var Q1;
            Q1=makeQuery(id+"F1.opExtrude","SWEPT_FACE",FACE,{"disambiguationData":[OSD([sQuery(id+"F0.wireOp",EDGE,"E8")])]});
            var Q2;
            Q2=makeQuery(id+"F1.opExtrude","SWEPT_FACE",FACE,{"disambiguationData":[OSD([sQuery(id+"F0.wireOp",EDGE,"E6")])]});
            extrude(context, id + "F7", {"entities" : qUnion([Q0]), "operationType" : NewBodyOperationType.ADD, "endBound" : BoundingType.UP_TO_SURFACE, "endBoundEntityFace" : qUnion([Q1]), "depth" : 25 * mm});
        }
        {
            var Q0;
            Q0=makeQuery(id+"F1.opExtrude","SWEPT_FACE",FACE,{"disambiguationData":[OSD([sQuery(id+"F0.wireOp",EDGE,"E6")])]});
            var sketch = newSketch(context, id + "F8", { "sketchPlane" : qUnion([Q0])});
            skLineSegment(sketch, "E49.0", {"start": v(40.67, 1.5) * mm, "end": v(40.67, 0) * mm});
            skArc(sketch, "E49.1", {"start": v(39.67, 1.5) * mm, "mid": v(40.17, 2) * mm, "end": v(40.67, 1.5) * mm});
            skLineSegment(sketch, "E49.2", {"start": v(39.67, 1.5) * mm, "end": v(39.67, 0) * mm});
            skLineSegment(sketch, "E50.0", {"start": v(19.33, 1.5) * mm, "end": v(19.33, 0) * mm});
            skArc(sketch, "E50.1", {"start": v(19.33, 1.5) * mm, "mid": v(19.83, 2) * mm, "end": v(20.33, 1.5) * mm});
            skLineSegment(sketch, "E50.2", {"start": v(20.33, 1.5) * mm, "end": v(20.33, 0) * mm});
            skLineSegment(sketch, "E51", {"start": v(19.33, 0) * mm, "end": v(20.33, 0) * mm});
            skLineSegment(sketch, "E52", {"start": v(39.67, 0) * mm, "end": v(40.67, 0) * mm});
            skSolve(sketch);
        }
        {
            var Q0;
            Q0=qSketchRegion(id+"F8",true);
            extrude(context, id + "F9", {"entities" : qUnion([Q0]), "operationType" : NewBodyOperationType.ADD, "endBound" : BoundingType.UP_TO_NEXT, "depth" : 25 * mm});
        }
        {
            var Q0;
            Q0=qCreatedBy(makeId("Front.planeOp"),FACE);
            var sketch = newSketch(context, id + "F10", { "sketchPlane" : qUnion([Q0])});
            skLineSegment(sketch, "E53", {"start": v(0, 0) * mm, "end": v(-40.81, 28.89) * mm});
            skLineSegment(sketch, "E54", {"start": v(-40.81, 28.89) * mm, "end": v(9.22, 99.57) * mm});
            skLineSegment(sketch, "E55", {"start": v(9.22, 99.57) * mm, "end": v(0, 0) * mm});
            skSolve(sketch);
        }
        {
            var Q0;
            Q0 = qSketchRegion(id + "F10", true);
            extrude(context, id + "F11", {"entities" : qUnion([Q0]), "operationType" : NewBodyOperationType.ADD, "depth" : 25 * mm});
        }
    });
